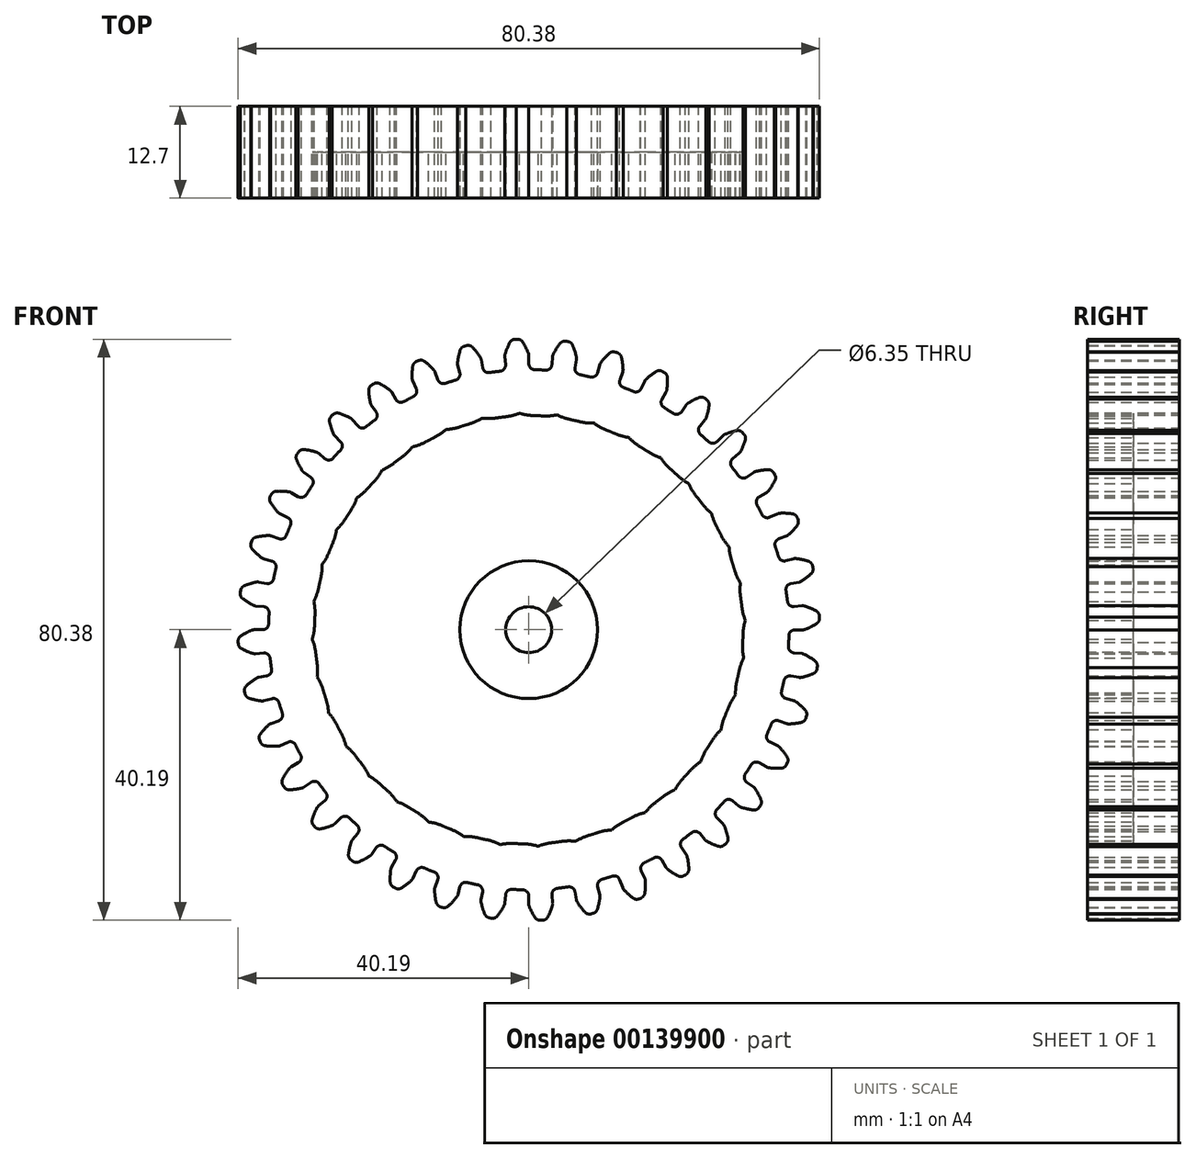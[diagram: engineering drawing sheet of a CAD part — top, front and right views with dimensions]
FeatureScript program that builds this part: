
annotation { "Feature Type Name" : "Feature", "Feature Type Description" : "" }
export const myFeature = defineFeature(function(context is Context, id is Id, definition is map)
    precondition{}
    {
        {
            assignVariable(context, id + "F0", {"name" : "CTA", "anyValue" : 5});
        }
        {
            var Q0;
            Q0=qCreatedBy(makeId("Front.planeOp"),FACE);
            var sketch = newSketch(context, id + "F1", { "sketchPlane" : qUnion([Q0])});
            skArc(sketch, "E0", {"start": v(-3.95, 35.77) * mm, "mid": v(-4.7, 35.68) * mm, "end": v(-5.44, 35.57) * mm});
            skArc(sketch, "E1.trimOffspring", {"start": v(-0.05, 38.25) * mm, "mid": v(-0.42, 39.05) * mm, "end": v(-0.86, 39.81) * mm});
            skLineSegment(sketch, "E2", {"start": v(-1.57, 40.2) * mm, "end": v(-1.75, 40.19) * mm});
            skLineSegment(sketch, "E3", {"start": v(0, 37.94) * mm, "end": v(0, 36.8) * mm});
            skLineSegment(sketch, "E4.MirrorCS", {"start": v(-1.93, 40.18) * mm, "end": v(-1.75, 40.19) * mm});
            skArc(sketch, "E5.MirrorCS", {"start": v(-3.28, 38.11) * mm, "mid": v(-2.99, 38.94) * mm, "end": v(-2.62, 39.74) * mm});
            skLineSegment(sketch, "E6.MirrorCS", {"start": v(-3.32, 37.8) * mm, "end": v(-3.22, 36.66) * mm});
            skPoint(sketch, "E7.visualSharp", {"position": v(-3.33, 37.95) * mm});
            skArc(sketch, "E7.filletArc", {"start": v(-3.28, 38.11) * mm, "mid": v(-3.31, 37.96) * mm, "end": v(-3.32, 37.8) * mm});
            skPoint(sketch, "E8.visualSharp", {"position": v(0, 38.1) * mm});
            skArc(sketch, "E8.filletArc", {"start": v(0, 37.94) * mm, "mid": v(0, 38.1) * mm, "end": v(-0.05, 38.25) * mm});
            skPoint(sketch, "E9.visualSharp", {"position": v(0, 35.98) * mm});
            skArc(sketch, "E9.filletArc", {"start": v(0, 36.8) * mm, "mid": v(0.24, 36.22) * mm, "end": v(0.82, 35.97) * mm});
            skPoint(sketch, "E10.visualSharp", {"position": v(-3.14, 35.85) * mm});
            skArc(sketch, "E10.filletArc", {"start": v(-3.95, 35.77) * mm, "mid": v(-3.4, 36.06) * mm, "end": v(-3.22, 36.66) * mm});
            skPoint(sketch, "E11.visualSharp", {"position": v(-2.39, 40.15) * mm});
            skArc(sketch, "E11.filletArc", {"start": v(-1.93, 40.18) * mm, "mid": v(-2.33, 40.05) * mm, "end": v(-2.62, 39.74) * mm});
            skPoint(sketch, "E12.visualSharp", {"position": v(-1.12, 40.2) * mm});
            skArc(sketch, "E12.filletArc", {"start": v(-0.86, 39.81) * mm, "mid": v(-1.17, 40.1) * mm, "end": v(-1.57, 40.2) * mm});
            skArc(sketch, "E13.1.0", {"start": v(-10.1, 34.54) * mm, "mid": v(-9.61, 34.92) * mm, "end": v(-9.53, 35.54) * mm});
            skLineSegment(sketch, "E13.1.1", {"start": v(-9.83, 36.65) * mm, "end": v(-9.53, 35.54) * mm});
            skArc(sketch, "E13.1.2", {"start": v(-9.85, 36.96) * mm, "mid": v(-9.7, 37.83) * mm, "end": v(-9.48, 38.68) * mm});
            skArc(sketch, "E13.1.3", {"start": v(-8.88, 39.23) * mm, "mid": v(-9.25, 39.03) * mm, "end": v(-9.48, 38.68) * mm});
            skLineSegment(sketch, "E13.1.4", {"start": v(-8.88, 39.23) * mm, "end": v(-8.7, 39.27) * mm});
            skLineSegment(sketch, "E13.1.5", {"start": v(-8.53, 39.3) * mm, "end": v(-8.7, 39.27) * mm});
            skArc(sketch, "E13.1.6", {"start": v(-7.76, 39.06) * mm, "mid": v(-8.11, 39.29) * mm, "end": v(-8.53, 39.3) * mm});
            skArc(sketch, "E13.1.7", {"start": v(-6.7, 37.66) * mm, "mid": v(-7.2, 38.39) * mm, "end": v(-7.76, 39.06) * mm});
            skLineSegment(sketch, "E13.1.8", {"start": v(-6.58, 37.37) * mm, "end": v(-6.38, 36.24) * mm});
            skArc(sketch, "E13.1.9", {"start": v(-6.38, 36.24) * mm, "mid": v(-6.05, 35.71) * mm, "end": v(-5.44, 35.57) * mm});
            skArc(sketch, "E13.1.10", {"start": v(-6.58, 37.37) * mm, "mid": v(-6.62, 37.52) * mm, "end": v(-6.7, 37.66) * mm});
            skPoint(sketch, "E13.1.11", {"position": v(-9.87, 36.8) * mm});
            skArc(sketch, "E13.1.12", {"start": v(-9.85, 36.96) * mm, "mid": v(-9.85, 36.8) * mm, "end": v(-9.83, 36.65) * mm});
            skArc(sketch, "E13.2.0", {"start": v(-15.94, 32.26) * mm, "mid": v(-15.53, 32.73) * mm, "end": v(-15.56, 33.35) * mm});
            skLineSegment(sketch, "E13.2.1", {"start": v(-16.04, 34.38) * mm, "end": v(-15.56, 33.35) * mm});
            skArc(sketch, "E13.2.2", {"start": v(-16.12, 34.7) * mm, "mid": v(-16.12, 35.57) * mm, "end": v(-16.05, 36.44) * mm});
            skArc(sketch, "E13.2.3", {"start": v(-15.56, 37.1) * mm, "mid": v(-15.89, 36.83) * mm, "end": v(-16.05, 36.44) * mm});
            skLineSegment(sketch, "E13.2.4", {"start": v(-15.56, 37.1) * mm, "end": v(-15.4, 37.16) * mm});
            skLineSegment(sketch, "E13.2.5", {"start": v(-15.23, 37.23) * mm, "end": v(-15.4, 37.16) * mm});
            skArc(sketch, "E13.2.6", {"start": v(-14.42, 37.12) * mm, "mid": v(-14.8, 37.28) * mm, "end": v(-15.23, 37.23) * mm});
            skArc(sketch, "E13.2.7", {"start": v(-13.13, 35.93) * mm, "mid": v(-13.75, 36.55) * mm, "end": v(-14.42, 37.12) * mm});
            skLineSegment(sketch, "E13.2.8", {"start": v(-12.97, 35.66) * mm, "end": v(-12.58, 34.58) * mm});
            skArc(sketch, "E13.2.9", {"start": v(-12.58, 34.58) * mm, "mid": v(-12.16, 34.12) * mm, "end": v(-11.54, 34.08) * mm});
            skArc(sketch, "E13.2.10", {"start": v(-12.97, 35.66) * mm, "mid": v(-13.04, 35.8) * mm, "end": v(-13.13, 35.93) * mm});
            skPoint(sketch, "E13.2.11", {"position": v(-16.1, 34.53) * mm});
            skArc(sketch, "E13.2.12", {"start": v(-16.12, 34.7) * mm, "mid": v(-16.1, 34.53) * mm, "end": v(-16.04, 34.38) * mm});
            skArc(sketch, "E13.3.0", {"start": v(-21.3, 29) * mm, "mid": v(-20.98, 29.53) * mm, "end": v(-21.11, 30.14) * mm});
            skLineSegment(sketch, "E13.3.1", {"start": v(-21.77, 31.08) * mm, "end": v(-21.11, 30.14) * mm});
            skArc(sketch, "E13.3.2", {"start": v(-21.9, 31.36) * mm, "mid": v(-22.06, 32.23) * mm, "end": v(-22.13, 33.1) * mm});
            skArc(sketch, "E13.3.3", {"start": v(-21.76, 33.83) * mm, "mid": v(-22.04, 33.51) * mm, "end": v(-22.13, 33.1) * mm});
            skLineSegment(sketch, "E13.3.4", {"start": v(-21.76, 33.83) * mm, "end": v(-21.61, 33.93) * mm});
            skLineSegment(sketch, "E13.3.5", {"start": v(-21.46, 34.02) * mm, "end": v(-21.61, 33.93) * mm});
            skArc(sketch, "E13.3.6", {"start": v(-20.65, 34.05) * mm, "mid": v(-21.06, 34.14) * mm, "end": v(-21.46, 34.02) * mm});
            skArc(sketch, "E13.3.7", {"start": v(-19.17, 33.1) * mm, "mid": v(-19.89, 33.61) * mm, "end": v(-20.65, 34.05) * mm});
            skLineSegment(sketch, "E13.3.8", {"start": v(-18.96, 32.86) * mm, "end": v(-18.4, 31.87) * mm});
            skArc(sketch, "E13.3.9", {"start": v(-18.4, 31.87) * mm, "mid": v(-17.9, 31.5) * mm, "end": v(-17.28, 31.56) * mm});
            skArc(sketch, "E13.3.10", {"start": v(-18.96, 32.86) * mm, "mid": v(-19.06, 33) * mm, "end": v(-19.17, 33.1) * mm});
            skPoint(sketch, "E13.3.11", {"position": v(-21.86, 31.2) * mm});
            skArc(sketch, "E13.3.12", {"start": v(-21.9, 31.36) * mm, "mid": v(-21.85, 31.21) * mm, "end": v(-21.77, 31.08) * mm});
            skArc(sketch, "E13.4.0", {"start": v(-26.01, 24.86) * mm, "mid": v(-25.79, 25.44) * mm, "end": v(-26.03, 26.01) * mm});
            skLineSegment(sketch, "E13.4.1", {"start": v(-26.84, 26.82) * mm, "end": v(-26.03, 26.01) * mm});
            skArc(sketch, "E13.4.2", {"start": v(-27.01, 27.09) * mm, "mid": v(-27.32, 27.9) * mm, "end": v(-27.55, 28.76) * mm});
            skArc(sketch, "E13.4.3", {"start": v(-27.3, 29.53) * mm, "mid": v(-27.53, 29.18) * mm, "end": v(-27.55, 28.76) * mm});
            skLineSegment(sketch, "E13.4.4", {"start": v(-27.3, 29.53) * mm, "end": v(-27.18, 29.66) * mm});
            skLineSegment(sketch, "E13.4.5", {"start": v(-27.04, 29.78) * mm, "end": v(-27.18, 29.66) * mm});
            skArc(sketch, "E13.4.6", {"start": v(-26.25, 29.95) * mm, "mid": v(-26.67, 29.97) * mm, "end": v(-27.04, 29.78) * mm});
            skArc(sketch, "E13.4.7", {"start": v(-24.63, 29.27) * mm, "mid": v(-25.42, 29.65) * mm, "end": v(-26.25, 29.95) * mm});
            skLineSegment(sketch, "E13.4.8", {"start": v(-24.38, 29.07) * mm, "end": v(-23.65, 28.2) * mm});
            skArc(sketch, "E13.4.9", {"start": v(-23.65, 28.2) * mm, "mid": v(-23.1, 27.9) * mm, "end": v(-22.5, 28.08) * mm});
            skArc(sketch, "E13.4.10", {"start": v(-24.38, 29.07) * mm, "mid": v(-24.5, 29.18) * mm, "end": v(-24.63, 29.27) * mm});
            skPoint(sketch, "E13.4.11", {"position": v(-26.95, 26.93) * mm});
            skArc(sketch, "E13.4.12", {"start": v(-27.01, 27.09) * mm, "mid": v(-26.94, 26.95) * mm, "end": v(-26.84, 26.82) * mm});
            skArc(sketch, "E13.5.0", {"start": v(-29.94, 19.97) * mm, "mid": v(-29.81, 20.58) * mm, "end": v(-30.15, 21.1) * mm});
            skLineSegment(sketch, "E13.5.1", {"start": v(-31.09, 21.76) * mm, "end": v(-30.15, 21.1) * mm});
            skArc(sketch, "E13.5.2", {"start": v(-31.3, 21.98) * mm, "mid": v(-31.75, 22.74) * mm, "end": v(-32.12, 23.54) * mm});
            skArc(sketch, "E13.5.3", {"start": v(-32.02, 24.34) * mm, "mid": v(-32.18, 23.95) * mm, "end": v(-32.12, 23.54) * mm});
            skLineSegment(sketch, "E13.5.4", {"start": v(-32.02, 24.34) * mm, "end": v(-31.91, 24.49) * mm});
            skLineSegment(sketch, "E13.5.5", {"start": v(-31.8, 24.63) * mm, "end": v(-31.91, 24.49) * mm});
            skArc(sketch, "E13.5.6", {"start": v(-31.05, 24.93) * mm, "mid": v(-31.47, 24.88) * mm, "end": v(-31.8, 24.63) * mm});
            skArc(sketch, "E13.5.7", {"start": v(-29.34, 24.55) * mm, "mid": v(-30.18, 24.78) * mm, "end": v(-31.05, 24.93) * mm});
            skLineSegment(sketch, "E13.5.8", {"start": v(-29.06, 24.4) * mm, "end": v(-28.18, 23.66) * mm});
            skArc(sketch, "E13.5.9", {"start": v(-28.18, 23.66) * mm, "mid": v(-27.6, 23.47) * mm, "end": v(-27.03, 23.75) * mm});
            skArc(sketch, "E13.5.10", {"start": v(-29.06, 24.4) * mm, "mid": v(-29.2, 24.49) * mm, "end": v(-29.34, 24.55) * mm});
            skPoint(sketch, "E13.5.11", {"position": v(-31.21, 21.85) * mm});
            skArc(sketch, "E13.5.12", {"start": v(-31.3, 21.98) * mm, "mid": v(-31.2, 21.86) * mm, "end": v(-31.09, 21.76) * mm});
            skArc(sketch, "E13.6.0", {"start": v(-32.95, 14.46) * mm, "mid": v(-32.93, 15.09) * mm, "end": v(-33.36, 15.54) * mm});
            skLineSegment(sketch, "E13.6.1", {"start": v(-34.4, 16.03) * mm, "end": v(-33.36, 15.54) * mm});
            skArc(sketch, "E13.6.2", {"start": v(-34.65, 16.21) * mm, "mid": v(-35.22, 16.88) * mm, "end": v(-35.72, 17.6) * mm});
            skArc(sketch, "E13.6.3", {"start": v(-35.76, 18.41) * mm, "mid": v(-35.85, 18) * mm, "end": v(-35.72, 17.6) * mm});
            skLineSegment(sketch, "E13.6.4", {"start": v(-35.76, 18.41) * mm, "end": v(-35.68, 18.57) * mm});
            skLineSegment(sketch, "E13.6.5", {"start": v(-35.6, 18.73) * mm, "end": v(-35.68, 18.57) * mm});
            skArc(sketch, "E13.6.6", {"start": v(-34.9, 19.16) * mm, "mid": v(-35.3, 19.04) * mm, "end": v(-35.6, 18.73) * mm});
            skArc(sketch, "E13.6.7", {"start": v(-33.15, 19.08) * mm, "mid": v(-34.03, 19.16) * mm, "end": v(-34.9, 19.16) * mm});
            skLineSegment(sketch, "E13.6.8", {"start": v(-32.86, 18.98) * mm, "end": v(-31.86, 18.4) * mm});
            skArc(sketch, "E13.6.9", {"start": v(-31.86, 18.4) * mm, "mid": v(-31.25, 18.32) * mm, "end": v(-30.75, 18.7) * mm});
            skArc(sketch, "E13.6.10", {"start": v(-32.86, 18.98) * mm, "mid": v(-33, 19.04) * mm, "end": v(-33.15, 19.08) * mm});
            skPoint(sketch, "E13.6.11", {"position": v(-34.53, 16.1) * mm});
            skArc(sketch, "E13.6.12", {"start": v(-34.65, 16.21) * mm, "mid": v(-34.53, 16.1) * mm, "end": v(-34.4, 16.03) * mm});
            skArc(sketch, "E13.7.0", {"start": v(-34.96, 8.52) * mm, "mid": v(-35.05, 9.14) * mm, "end": v(-35.55, 9.52) * mm});
            skLineSegment(sketch, "E13.7.1", {"start": v(-36.65, 9.81) * mm, "end": v(-35.55, 9.52) * mm});
            skArc(sketch, "E13.7.2", {"start": v(-36.94, 9.95) * mm, "mid": v(-37.61, 10.51) * mm, "end": v(-38.23, 11.13) * mm});
            skArc(sketch, "E13.7.3", {"start": v(-38.42, 11.92) * mm, "mid": v(-38.43, 11.5) * mm, "end": v(-38.23, 11.13) * mm});
            skLineSegment(sketch, "E13.7.4", {"start": v(-38.42, 11.92) * mm, "end": v(-38.36, 12.1) * mm});
            skLineSegment(sketch, "E13.7.5", {"start": v(-38.3, 12.27) * mm, "end": v(-38.36, 12.1) * mm});
            skArc(sketch, "E13.7.6", {"start": v(-37.7, 12.81) * mm, "mid": v(-38.08, 12.62) * mm, "end": v(-38.3, 12.27) * mm});
            skArc(sketch, "E13.7.7", {"start": v(-35.96, 13.03) * mm, "mid": v(-36.84, 12.96) * mm, "end": v(-37.7, 12.81) * mm});
            skLineSegment(sketch, "E13.7.8", {"start": v(-35.65, 12.99) * mm, "end": v(-34.58, 12.6) * mm});
            skArc(sketch, "E13.7.9", {"start": v(-34.58, 12.6) * mm, "mid": v(-33.95, 12.62) * mm, "end": v(-33.53, 13.07) * mm});
            skArc(sketch, "E13.7.10", {"start": v(-35.65, 12.99) * mm, "mid": v(-35.8, 13.03) * mm, "end": v(-35.96, 13.03) * mm});
            skPoint(sketch, "E13.7.11", {"position": v(-36.8, 9.85) * mm});
            skArc(sketch, "E13.7.12", {"start": v(-36.94, 9.95) * mm, "mid": v(-36.8, 9.87) * mm, "end": v(-36.65, 9.81) * mm});
            skArc(sketch, "E13.8.0", {"start": v(-35.9, 2.32) * mm, "mid": v(-36.1, 2.91) * mm, "end": v(-36.66, 3.2) * mm});
            skLineSegment(sketch, "E13.8.1", {"start": v(-37.8, 3.3) * mm, "end": v(-36.66, 3.2) * mm});
            skArc(sketch, "E13.8.2", {"start": v(-38.1, 3.39) * mm, "mid": v(-38.87, 3.82) * mm, "end": v(-39.59, 4.32) * mm});
            skArc(sketch, "E13.8.3", {"start": v(-39.9, 5.07) * mm, "mid": v(-39.84, 4.66) * mm, "end": v(-39.59, 4.32) * mm});
            skLineSegment(sketch, "E13.8.4", {"start": v(-39.9, 5.07) * mm, "end": v(-39.88, 5.25) * mm});
            skLineSegment(sketch, "E13.8.5", {"start": v(-39.86, 5.43) * mm, "end": v(-39.88, 5.25) * mm});
            skArc(sketch, "E13.8.6", {"start": v(-39.36, 6.07) * mm, "mid": v(-39.7, 5.82) * mm, "end": v(-39.86, 5.43) * mm});
            skArc(sketch, "E13.8.7", {"start": v(-37.68, 6.6) * mm, "mid": v(-38.53, 6.37) * mm, "end": v(-39.36, 6.07) * mm});
            skLineSegment(sketch, "E13.8.8", {"start": v(-37.37, 6.6) * mm, "end": v(-36.24, 6.4) * mm});
            skArc(sketch, "E13.8.9", {"start": v(-36.24, 6.4) * mm, "mid": v(-35.63, 6.53) * mm, "end": v(-35.29, 7.05) * mm});
            skArc(sketch, "E13.8.10", {"start": v(-37.37, 6.6) * mm, "mid": v(-37.52, 6.6) * mm, "end": v(-37.68, 6.6) * mm});
            skPoint(sketch, "E13.8.11", {"position": v(-37.96, 3.31) * mm});
            skArc(sketch, "E13.8.12", {"start": v(-38.1, 3.39) * mm, "mid": v(-37.96, 3.33) * mm, "end": v(-37.8, 3.3) * mm});
            skArc(sketch, "E13.9.0", {"start": v(-35.77, -3.95) * mm, "mid": v(-36.06, -3.4) * mm, "end": v(-36.66, -3.22) * mm});
            skLineSegment(sketch, "E13.9.1", {"start": v(-37.8, -3.32) * mm, "end": v(-36.66, -3.22) * mm});
            skArc(sketch, "E13.9.2", {"start": v(-38.11, -3.28) * mm, "mid": v(-38.94, -2.99) * mm, "end": v(-39.74, -2.62) * mm});
            skArc(sketch, "E13.9.3", {"start": v(-40.18, -1.93) * mm, "mid": v(-40.05, -2.33) * mm, "end": v(-39.74, -2.62) * mm});
            skLineSegment(sketch, "E13.9.4", {"start": v(-40.18, -1.93) * mm, "end": v(-40.19, -1.75) * mm});
            skLineSegment(sketch, "E13.9.5", {"start": v(-40.2, -1.57) * mm, "end": v(-40.19, -1.75) * mm});
            skArc(sketch, "E13.9.6", {"start": v(-39.81, -0.86) * mm, "mid": v(-40.1, -1.17) * mm, "end": v(-40.2, -1.57) * mm});
            skArc(sketch, "E13.9.7", {"start": v(-38.25, -0.05) * mm, "mid": v(-39.05, -0.42) * mm, "end": v(-39.81, -0.86) * mm});
            skLineSegment(sketch, "E13.9.8", {"start": v(-37.94, 0) * mm, "end": v(-36.8, 0) * mm});
            skArc(sketch, "E13.9.9", {"start": v(-36.8, 0) * mm, "mid": v(-36.22, 0.24) * mm, "end": v(-35.97, 0.82) * mm});
            skArc(sketch, "E13.9.10", {"start": v(-37.94, 0) * mm, "mid": v(-38.1, 0) * mm, "end": v(-38.25, -0.05) * mm});
            skPoint(sketch, "E13.9.11", {"position": v(-37.95, -3.33) * mm});
            skArc(sketch, "E13.9.12", {"start": v(-38.11, -3.28) * mm, "mid": v(-37.96, -3.31) * mm, "end": v(-37.8, -3.32) * mm});
            skArc(sketch, "E13.10.0", {"start": v(-34.54, -10.1) * mm, "mid": v(-34.92, -9.61) * mm, "end": v(-35.54, -9.53) * mm});
            skLineSegment(sketch, "E13.10.1", {"start": v(-36.65, -9.83) * mm, "end": v(-35.54, -9.53) * mm});
            skArc(sketch, "E13.10.2", {"start": v(-36.96, -9.85) * mm, "mid": v(-37.83, -9.7) * mm, "end": v(-38.68, -9.48) * mm});
            skArc(sketch, "E13.10.3", {"start": v(-39.23, -8.88) * mm, "mid": v(-39.03, -9.25) * mm, "end": v(-38.68, -9.48) * mm});
            skLineSegment(sketch, "E13.10.4", {"start": v(-39.23, -8.88) * mm, "end": v(-39.27, -8.7) * mm});
            skLineSegment(sketch, "E13.10.5", {"start": v(-39.3, -8.53) * mm, "end": v(-39.27, -8.7) * mm});
            skArc(sketch, "E13.10.6", {"start": v(-39.06, -7.76) * mm, "mid": v(-39.29, -8.11) * mm, "end": v(-39.3, -8.53) * mm});
            skArc(sketch, "E13.10.7", {"start": v(-37.66, -6.7) * mm, "mid": v(-38.39, -7.2) * mm, "end": v(-39.06, -7.76) * mm});
            skLineSegment(sketch, "E13.10.8", {"start": v(-37.37, -6.58) * mm, "end": v(-36.24, -6.38) * mm});
            skArc(sketch, "E13.10.9", {"start": v(-36.24, -6.38) * mm, "mid": v(-35.71, -6.05) * mm, "end": v(-35.57, -5.44) * mm});
            skArc(sketch, "E13.10.10", {"start": v(-37.37, -6.58) * mm, "mid": v(-37.52, -6.62) * mm, "end": v(-37.66, -6.7) * mm});
            skPoint(sketch, "E13.10.11", {"position": v(-36.8, -9.87) * mm});
            skArc(sketch, "E13.10.12", {"start": v(-36.96, -9.85) * mm, "mid": v(-36.8, -9.85) * mm, "end": v(-36.65, -9.83) * mm});
            skArc(sketch, "E13.11.0", {"start": v(-32.26, -15.94) * mm, "mid": v(-32.73, -15.53) * mm, "end": v(-33.35, -15.56) * mm});
            skLineSegment(sketch, "E13.11.1", {"start": v(-34.38, -16.04) * mm, "end": v(-33.35, -15.56) * mm});
            skArc(sketch, "E13.11.2", {"start": v(-34.7, -16.12) * mm, "mid": v(-35.57, -16.12) * mm, "end": v(-36.44, -16.05) * mm});
            skArc(sketch, "E13.11.3", {"start": v(-37.1, -15.56) * mm, "mid": v(-36.83, -15.89) * mm, "end": v(-36.44, -16.05) * mm});
            skLineSegment(sketch, "E13.11.4", {"start": v(-37.1, -15.56) * mm, "end": v(-37.16, -15.4) * mm});
            skLineSegment(sketch, "E13.11.5", {"start": v(-37.23, -15.23) * mm, "end": v(-37.16, -15.4) * mm});
            skArc(sketch, "E13.11.6", {"start": v(-37.12, -14.42) * mm, "mid": v(-37.28, -14.8) * mm, "end": v(-37.23, -15.23) * mm});
            skArc(sketch, "E13.11.7", {"start": v(-35.93, -13.13) * mm, "mid": v(-36.55, -13.75) * mm, "end": v(-37.12, -14.42) * mm});
            skLineSegment(sketch, "E13.11.8", {"start": v(-35.66, -12.97) * mm, "end": v(-34.58, -12.58) * mm});
            skArc(sketch, "E13.11.9", {"start": v(-34.58, -12.58) * mm, "mid": v(-34.12, -12.16) * mm, "end": v(-34.08, -11.54) * mm});
            skArc(sketch, "E13.11.10", {"start": v(-35.66, -12.97) * mm, "mid": v(-35.8, -13.04) * mm, "end": v(-35.93, -13.13) * mm});
            skPoint(sketch, "E13.11.11", {"position": v(-34.53, -16.1) * mm});
            skArc(sketch, "E13.11.12", {"start": v(-34.7, -16.12) * mm, "mid": v(-34.53, -16.1) * mm, "end": v(-34.38, -16.04) * mm});
            skArc(sketch, "E13.12.0", {"start": v(-29, -21.3) * mm, "mid": v(-29.53, -20.98) * mm, "end": v(-30.14, -21.11) * mm});
            skLineSegment(sketch, "E13.12.1", {"start": v(-31.08, -21.77) * mm, "end": v(-30.14, -21.11) * mm});
            skArc(sketch, "E13.12.2", {"start": v(-31.36, -21.9) * mm, "mid": v(-32.23, -22.06) * mm, "end": v(-33.1, -22.13) * mm});
            skArc(sketch, "E13.12.3", {"start": v(-33.83, -21.76) * mm, "mid": v(-33.51, -22.04) * mm, "end": v(-33.1, -22.13) * mm});
            skLineSegment(sketch, "E13.12.4", {"start": v(-33.83, -21.76) * mm, "end": v(-33.93, -21.61) * mm});
            skLineSegment(sketch, "E13.12.5", {"start": v(-34.02, -21.46) * mm, "end": v(-33.93, -21.61) * mm});
            skArc(sketch, "E13.12.6", {"start": v(-34.05, -20.65) * mm, "mid": v(-34.14, -21.06) * mm, "end": v(-34.02, -21.46) * mm});
            skArc(sketch, "E13.12.7", {"start": v(-33.1, -19.17) * mm, "mid": v(-33.61, -19.89) * mm, "end": v(-34.05, -20.65) * mm});
            skLineSegment(sketch, "E13.12.8", {"start": v(-32.86, -18.96) * mm, "end": v(-31.87, -18.4) * mm});
            skArc(sketch, "E13.12.9", {"start": v(-31.87, -18.4) * mm, "mid": v(-31.5, -17.9) * mm, "end": v(-31.56, -17.28) * mm});
            skArc(sketch, "E13.12.10", {"start": v(-32.86, -18.96) * mm, "mid": v(-33, -19.06) * mm, "end": v(-33.1, -19.17) * mm});
            skPoint(sketch, "E13.12.11", {"position": v(-31.2, -21.86) * mm});
            skArc(sketch, "E13.12.12", {"start": v(-31.36, -21.9) * mm, "mid": v(-31.21, -21.85) * mm, "end": v(-31.08, -21.77) * mm});
            skArc(sketch, "E13.13.0", {"start": v(-24.86, -26.01) * mm, "mid": v(-25.44, -25.79) * mm, "end": v(-26.01, -26.03) * mm});
            skLineSegment(sketch, "E13.13.1", {"start": v(-26.82, -26.84) * mm, "end": v(-26.01, -26.03) * mm});
            skArc(sketch, "E13.13.2", {"start": v(-27.09, -27.01) * mm, "mid": v(-27.9, -27.32) * mm, "end": v(-28.76, -27.55) * mm});
            skArc(sketch, "E13.13.3", {"start": v(-29.53, -27.3) * mm, "mid": v(-29.18, -27.53) * mm, "end": v(-28.76, -27.55) * mm});
            skLineSegment(sketch, "E13.13.4", {"start": v(-29.53, -27.3) * mm, "end": v(-29.66, -27.18) * mm});
            skLineSegment(sketch, "E13.13.5", {"start": v(-29.78, -27.04) * mm, "end": v(-29.66, -27.18) * mm});
            skArc(sketch, "E13.13.6", {"start": v(-29.95, -26.25) * mm, "mid": v(-29.97, -26.67) * mm, "end": v(-29.78, -27.04) * mm});
            skArc(sketch, "E13.13.7", {"start": v(-29.27, -24.63) * mm, "mid": v(-29.65, -25.42) * mm, "end": v(-29.95, -26.25) * mm});
            skLineSegment(sketch, "E13.13.8", {"start": v(-29.07, -24.38) * mm, "end": v(-28.2, -23.65) * mm});
            skArc(sketch, "E13.13.9", {"start": v(-28.2, -23.65) * mm, "mid": v(-27.9, -23.1) * mm, "end": v(-28.08, -22.5) * mm});
            skArc(sketch, "E13.13.10", {"start": v(-29.07, -24.38) * mm, "mid": v(-29.18, -24.5) * mm, "end": v(-29.27, -24.63) * mm});
            skPoint(sketch, "E13.13.11", {"position": v(-26.93, -26.95) * mm});
            skArc(sketch, "E13.13.12", {"start": v(-27.09, -27.01) * mm, "mid": v(-26.95, -26.94) * mm, "end": v(-26.82, -26.84) * mm});
            skArc(sketch, "E13.14.0", {"start": v(-19.97, -29.94) * mm, "mid": v(-20.58, -29.81) * mm, "end": v(-21.1, -30.15) * mm});
            skLineSegment(sketch, "E13.14.1", {"start": v(-21.76, -31.09) * mm, "end": v(-21.1, -30.15) * mm});
            skArc(sketch, "E13.14.2", {"start": v(-21.98, -31.3) * mm, "mid": v(-22.74, -31.75) * mm, "end": v(-23.54, -32.12) * mm});
            skArc(sketch, "E13.14.3", {"start": v(-24.34, -32.02) * mm, "mid": v(-23.95, -32.18) * mm, "end": v(-23.54, -32.12) * mm});
            skLineSegment(sketch, "E13.14.4", {"start": v(-24.34, -32.02) * mm, "end": v(-24.49, -31.91) * mm});
            skLineSegment(sketch, "E13.14.5", {"start": v(-24.63, -31.8) * mm, "end": v(-24.49, -31.91) * mm});
            skArc(sketch, "E13.14.6", {"start": v(-24.93, -31.05) * mm, "mid": v(-24.88, -31.47) * mm, "end": v(-24.63, -31.8) * mm});
            skArc(sketch, "E13.14.7", {"start": v(-24.55, -29.34) * mm, "mid": v(-24.78, -30.18) * mm, "end": v(-24.93, -31.05) * mm});
            skLineSegment(sketch, "E13.14.8", {"start": v(-24.4, -29.06) * mm, "end": v(-23.66, -28.18) * mm});
            skArc(sketch, "E13.14.9", {"start": v(-23.66, -28.18) * mm, "mid": v(-23.47, -27.6) * mm, "end": v(-23.75, -27.03) * mm});
            skArc(sketch, "E13.14.10", {"start": v(-24.4, -29.06) * mm, "mid": v(-24.49, -29.2) * mm, "end": v(-24.55, -29.34) * mm});
            skPoint(sketch, "E13.14.11", {"position": v(-21.85, -31.21) * mm});
            skArc(sketch, "E13.14.12", {"start": v(-21.98, -31.3) * mm, "mid": v(-21.86, -31.2) * mm, "end": v(-21.76, -31.09) * mm});
            skArc(sketch, "E13.15.0", {"start": v(-14.46, -32.95) * mm, "mid": v(-15.09, -32.93) * mm, "end": v(-15.54, -33.36) * mm});
            skLineSegment(sketch, "E13.15.1", {"start": v(-16.03, -34.4) * mm, "end": v(-15.54, -33.36) * mm});
            skArc(sketch, "E13.15.2", {"start": v(-16.21, -34.65) * mm, "mid": v(-16.88, -35.22) * mm, "end": v(-17.6, -35.72) * mm});
            skArc(sketch, "E13.15.3", {"start": v(-18.41, -35.76) * mm, "mid": v(-18, -35.85) * mm, "end": v(-17.6, -35.72) * mm});
            skLineSegment(sketch, "E13.15.4", {"start": v(-18.41, -35.76) * mm, "end": v(-18.57, -35.68) * mm});
            skLineSegment(sketch, "E13.15.5", {"start": v(-18.73, -35.6) * mm, "end": v(-18.57, -35.68) * mm});
            skArc(sketch, "E13.15.6", {"start": v(-19.16, -34.9) * mm, "mid": v(-19.04, -35.3) * mm, "end": v(-18.73, -35.6) * mm});
            skArc(sketch, "E13.15.7", {"start": v(-19.08, -33.15) * mm, "mid": v(-19.16, -34.03) * mm, "end": v(-19.16, -34.9) * mm});
            skLineSegment(sketch, "E13.15.8", {"start": v(-18.98, -32.86) * mm, "end": v(-18.4, -31.86) * mm});
            skArc(sketch, "E13.15.9", {"start": v(-18.4, -31.86) * mm, "mid": v(-18.32, -31.25) * mm, "end": v(-18.7, -30.75) * mm});
            skArc(sketch, "E13.15.10", {"start": v(-18.98, -32.86) * mm, "mid": v(-19.04, -33) * mm, "end": v(-19.08, -33.15) * mm});
            skPoint(sketch, "E13.15.11", {"position": v(-16.1, -34.53) * mm});
            skArc(sketch, "E13.15.12", {"start": v(-16.21, -34.65) * mm, "mid": v(-16.1, -34.53) * mm, "end": v(-16.03, -34.4) * mm});
            skArc(sketch, "E13.16.0", {"start": v(-8.52, -34.96) * mm, "mid": v(-9.14, -35.05) * mm, "end": v(-9.52, -35.55) * mm});
            skLineSegment(sketch, "E13.16.1", {"start": v(-9.81, -36.65) * mm, "end": v(-9.52, -35.55) * mm});
            skArc(sketch, "E13.16.2", {"start": v(-9.95, -36.94) * mm, "mid": v(-10.51, -37.61) * mm, "end": v(-11.13, -38.23) * mm});
            skArc(sketch, "E13.16.3", {"start": v(-11.92, -38.42) * mm, "mid": v(-11.5, -38.43) * mm, "end": v(-11.13, -38.23) * mm});
            skLineSegment(sketch, "E13.16.4", {"start": v(-11.92, -38.42) * mm, "end": v(-12.1, -38.36) * mm});
            skLineSegment(sketch, "E13.16.5", {"start": v(-12.27, -38.3) * mm, "end": v(-12.1, -38.36) * mm});
            skArc(sketch, "E13.16.6", {"start": v(-12.81, -37.7) * mm, "mid": v(-12.62, -38.08) * mm, "end": v(-12.27, -38.3) * mm});
            skArc(sketch, "E13.16.7", {"start": v(-13.03, -35.96) * mm, "mid": v(-12.96, -36.84) * mm, "end": v(-12.81, -37.7) * mm});
            skLineSegment(sketch, "E13.16.8", {"start": v(-12.99, -35.65) * mm, "end": v(-12.6, -34.58) * mm});
            skArc(sketch, "E13.16.9", {"start": v(-12.6, -34.58) * mm, "mid": v(-12.62, -33.95) * mm, "end": v(-13.07, -33.53) * mm});
            skArc(sketch, "E13.16.10", {"start": v(-12.99, -35.65) * mm, "mid": v(-13.03, -35.8) * mm, "end": v(-13.03, -35.96) * mm});
            skPoint(sketch, "E13.16.11", {"position": v(-9.85, -36.8) * mm});
            skArc(sketch, "E13.16.12", {"start": v(-9.95, -36.94) * mm, "mid": v(-9.87, -36.8) * mm, "end": v(-9.81, -36.65) * mm});
            skArc(sketch, "E13.17.0", {"start": v(-2.32, -35.9) * mm, "mid": v(-2.91, -36.1) * mm, "end": v(-3.2, -36.66) * mm});
            skLineSegment(sketch, "E13.17.1", {"start": v(-3.3, -37.8) * mm, "end": v(-3.2, -36.66) * mm});
            skArc(sketch, "E13.17.2", {"start": v(-3.39, -38.1) * mm, "mid": v(-3.82, -38.87) * mm, "end": v(-4.32, -39.59) * mm});
            skArc(sketch, "E13.17.3", {"start": v(-5.07, -39.9) * mm, "mid": v(-4.66, -39.84) * mm, "end": v(-4.32, -39.59) * mm});
            skLineSegment(sketch, "E13.17.4", {"start": v(-5.07, -39.9) * mm, "end": v(-5.25, -39.88) * mm});
            skLineSegment(sketch, "E13.17.5", {"start": v(-5.43, -39.86) * mm, "end": v(-5.25, -39.88) * mm});
            skArc(sketch, "E13.17.6", {"start": v(-6.07, -39.36) * mm, "mid": v(-5.82, -39.7) * mm, "end": v(-5.43, -39.86) * mm});
            skArc(sketch, "E13.17.7", {"start": v(-6.6, -37.68) * mm, "mid": v(-6.37, -38.53) * mm, "end": v(-6.07, -39.36) * mm});
            skLineSegment(sketch, "E13.17.8", {"start": v(-6.6, -37.37) * mm, "end": v(-6.4, -36.24) * mm});
            skArc(sketch, "E13.17.9", {"start": v(-6.4, -36.24) * mm, "mid": v(-6.53, -35.63) * mm, "end": v(-7.05, -35.29) * mm});
            skArc(sketch, "E13.17.10", {"start": v(-6.6, -37.37) * mm, "mid": v(-6.6, -37.52) * mm, "end": v(-6.6, -37.68) * mm});
            skPoint(sketch, "E13.17.11", {"position": v(-3.31, -37.96) * mm});
            skArc(sketch, "E13.17.12", {"start": v(-3.39, -38.1) * mm, "mid": v(-3.33, -37.96) * mm, "end": v(-3.3, -37.8) * mm});
            skArc(sketch, "E13.18.0", {"start": v(3.95, -35.77) * mm, "mid": v(3.4, -36.06) * mm, "end": v(3.22, -36.66) * mm});
            skLineSegment(sketch, "E13.18.1", {"start": v(3.32, -37.8) * mm, "end": v(3.22, -36.66) * mm});
            skArc(sketch, "E13.18.2", {"start": v(3.28, -38.11) * mm, "mid": v(2.99, -38.94) * mm, "end": v(2.62, -39.74) * mm});
            skArc(sketch, "E13.18.3", {"start": v(1.93, -40.18) * mm, "mid": v(2.33, -40.05) * mm, "end": v(2.62, -39.74) * mm});
            skLineSegment(sketch, "E13.18.4", {"start": v(1.93, -40.18) * mm, "end": v(1.75, -40.19) * mm});
            skLineSegment(sketch, "E13.18.5", {"start": v(1.57, -40.2) * mm, "end": v(1.75, -40.19) * mm});
            skArc(sketch, "E13.18.6", {"start": v(0.86, -39.81) * mm, "mid": v(1.17, -40.1) * mm, "end": v(1.57, -40.2) * mm});
            skArc(sketch, "E13.18.7", {"start": v(0.05, -38.25) * mm, "mid": v(0.42, -39.05) * mm, "end": v(0.86, -39.81) * mm});
            skLineSegment(sketch, "E13.18.8", {"start": v(0, -37.94) * mm, "end": v(0, -36.8) * mm});
            skArc(sketch, "E13.18.9", {"start": v(0, -36.8) * mm, "mid": v(-0.24, -36.22) * mm, "end": v(-0.82, -35.97) * mm});
            skArc(sketch, "E13.18.10", {"start": v(0, -37.94) * mm, "mid": v(0, -38.1) * mm, "end": v(0.05, -38.25) * mm});
            skPoint(sketch, "E13.18.11", {"position": v(3.33, -37.95) * mm});
            skArc(sketch, "E13.18.12", {"start": v(3.28, -38.11) * mm, "mid": v(3.31, -37.96) * mm, "end": v(3.32, -37.8) * mm});
            skArc(sketch, "E13.19.0", {"start": v(10.1, -34.54) * mm, "mid": v(9.61, -34.92) * mm, "end": v(9.53, -35.54) * mm});
            skLineSegment(sketch, "E13.19.1", {"start": v(9.83, -36.65) * mm, "end": v(9.53, -35.54) * mm});
            skArc(sketch, "E13.19.2", {"start": v(9.85, -36.96) * mm, "mid": v(9.7, -37.83) * mm, "end": v(9.48, -38.68) * mm});
            skArc(sketch, "E13.19.3", {"start": v(8.88, -39.23) * mm, "mid": v(9.25, -39.03) * mm, "end": v(9.48, -38.68) * mm});
            skLineSegment(sketch, "E13.19.4", {"start": v(8.88, -39.23) * mm, "end": v(8.7, -39.27) * mm});
            skLineSegment(sketch, "E13.19.5", {"start": v(8.53, -39.3) * mm, "end": v(8.7, -39.27) * mm});
            skArc(sketch, "E13.19.6", {"start": v(7.76, -39.06) * mm, "mid": v(8.11, -39.29) * mm, "end": v(8.53, -39.3) * mm});
            skArc(sketch, "E13.19.7", {"start": v(6.7, -37.66) * mm, "mid": v(7.2, -38.39) * mm, "end": v(7.76, -39.06) * mm});
            skLineSegment(sketch, "E13.19.8", {"start": v(6.58, -37.37) * mm, "end": v(6.38, -36.24) * mm});
            skArc(sketch, "E13.19.9", {"start": v(6.38, -36.24) * mm, "mid": v(6.05, -35.71) * mm, "end": v(5.44, -35.57) * mm});
            skArc(sketch, "E13.19.10", {"start": v(6.58, -37.37) * mm, "mid": v(6.62, -37.52) * mm, "end": v(6.7, -37.66) * mm});
            skPoint(sketch, "E13.19.11", {"position": v(9.87, -36.8) * mm});
            skArc(sketch, "E13.19.12", {"start": v(9.85, -36.96) * mm, "mid": v(9.85, -36.8) * mm, "end": v(9.83, -36.65) * mm});
            skArc(sketch, "E13.20.0", {"start": v(15.94, -32.26) * mm, "mid": v(15.53, -32.73) * mm, "end": v(15.56, -33.35) * mm});
            skLineSegment(sketch, "E13.20.1", {"start": v(16.04, -34.38) * mm, "end": v(15.56, -33.35) * mm});
            skArc(sketch, "E13.20.2", {"start": v(16.12, -34.7) * mm, "mid": v(16.12, -35.57) * mm, "end": v(16.05, -36.44) * mm});
            skArc(sketch, "E13.20.3", {"start": v(15.56, -37.1) * mm, "mid": v(15.89, -36.83) * mm, "end": v(16.05, -36.44) * mm});
            skLineSegment(sketch, "E13.20.4", {"start": v(15.56, -37.1) * mm, "end": v(15.4, -37.16) * mm});
            skLineSegment(sketch, "E13.20.5", {"start": v(15.23, -37.23) * mm, "end": v(15.4, -37.16) * mm});
            skArc(sketch, "E13.20.6", {"start": v(14.42, -37.12) * mm, "mid": v(14.8, -37.28) * mm, "end": v(15.23, -37.23) * mm});
            skArc(sketch, "E13.20.7", {"start": v(13.13, -35.93) * mm, "mid": v(13.75, -36.55) * mm, "end": v(14.42, -37.12) * mm});
            skLineSegment(sketch, "E13.20.8", {"start": v(12.97, -35.66) * mm, "end": v(12.58, -34.58) * mm});
            skArc(sketch, "E13.20.9", {"start": v(12.58, -34.58) * mm, "mid": v(12.16, -34.12) * mm, "end": v(11.54, -34.08) * mm});
            skArc(sketch, "E13.20.10", {"start": v(12.97, -35.66) * mm, "mid": v(13.04, -35.8) * mm, "end": v(13.13, -35.93) * mm});
            skPoint(sketch, "E13.20.11", {"position": v(16.1, -34.53) * mm});
            skArc(sketch, "E13.20.12", {"start": v(16.12, -34.7) * mm, "mid": v(16.1, -34.53) * mm, "end": v(16.04, -34.38) * mm});
            skArc(sketch, "E13.21.0", {"start": v(21.3, -29) * mm, "mid": v(20.98, -29.53) * mm, "end": v(21.11, -30.14) * mm});
            skLineSegment(sketch, "E13.21.1", {"start": v(21.77, -31.08) * mm, "end": v(21.11, -30.14) * mm});
            skArc(sketch, "E13.21.2", {"start": v(21.9, -31.36) * mm, "mid": v(22.06, -32.23) * mm, "end": v(22.13, -33.1) * mm});
            skArc(sketch, "E13.21.3", {"start": v(21.76, -33.83) * mm, "mid": v(22.04, -33.51) * mm, "end": v(22.13, -33.1) * mm});
            skLineSegment(sketch, "E13.21.4", {"start": v(21.76, -33.83) * mm, "end": v(21.61, -33.93) * mm});
            skLineSegment(sketch, "E13.21.5", {"start": v(21.46, -34.02) * mm, "end": v(21.61, -33.93) * mm});
            skArc(sketch, "E13.21.6", {"start": v(20.65, -34.05) * mm, "mid": v(21.06, -34.14) * mm, "end": v(21.46, -34.02) * mm});
            skArc(sketch, "E13.21.7", {"start": v(19.17, -33.1) * mm, "mid": v(19.89, -33.61) * mm, "end": v(20.65, -34.05) * mm});
            skLineSegment(sketch, "E13.21.8", {"start": v(18.96, -32.86) * mm, "end": v(18.4, -31.87) * mm});
            skArc(sketch, "E13.21.9", {"start": v(18.4, -31.87) * mm, "mid": v(17.9, -31.5) * mm, "end": v(17.28, -31.56) * mm});
            skArc(sketch, "E13.21.10", {"start": v(18.96, -32.86) * mm, "mid": v(19.06, -33) * mm, "end": v(19.17, -33.1) * mm});
            skPoint(sketch, "E13.21.11", {"position": v(21.86, -31.2) * mm});
            skArc(sketch, "E13.21.12", {"start": v(21.9, -31.36) * mm, "mid": v(21.85, -31.21) * mm, "end": v(21.77, -31.08) * mm});
            skArc(sketch, "E13.22.0", {"start": v(26.01, -24.86) * mm, "mid": v(25.79, -25.44) * mm, "end": v(26.03, -26.01) * mm});
            skLineSegment(sketch, "E13.22.1", {"start": v(26.84, -26.82) * mm, "end": v(26.03, -26.01) * mm});
            skArc(sketch, "E13.22.2", {"start": v(27.01, -27.09) * mm, "mid": v(27.32, -27.9) * mm, "end": v(27.55, -28.76) * mm});
            skArc(sketch, "E13.22.3", {"start": v(27.3, -29.53) * mm, "mid": v(27.53, -29.18) * mm, "end": v(27.55, -28.76) * mm});
            skLineSegment(sketch, "E13.22.4", {"start": v(27.3, -29.53) * mm, "end": v(27.18, -29.66) * mm});
            skLineSegment(sketch, "E13.22.5", {"start": v(27.04, -29.78) * mm, "end": v(27.18, -29.66) * mm});
            skArc(sketch, "E13.22.6", {"start": v(26.25, -29.95) * mm, "mid": v(26.67, -29.97) * mm, "end": v(27.04, -29.78) * mm});
            skArc(sketch, "E13.22.7", {"start": v(24.63, -29.27) * mm, "mid": v(25.42, -29.65) * mm, "end": v(26.25, -29.95) * mm});
            skLineSegment(sketch, "E13.22.8", {"start": v(24.38, -29.07) * mm, "end": v(23.65, -28.2) * mm});
            skArc(sketch, "E13.22.9", {"start": v(23.65, -28.2) * mm, "mid": v(23.1, -27.9) * mm, "end": v(22.5, -28.08) * mm});
            skArc(sketch, "E13.22.10", {"start": v(24.38, -29.07) * mm, "mid": v(24.5, -29.18) * mm, "end": v(24.63, -29.27) * mm});
            skPoint(sketch, "E13.22.11", {"position": v(26.95, -26.93) * mm});
            skArc(sketch, "E13.22.12", {"start": v(27.01, -27.09) * mm, "mid": v(26.94, -26.95) * mm, "end": v(26.84, -26.82) * mm});
            skArc(sketch, "E13.23.0", {"start": v(29.94, -19.97) * mm, "mid": v(29.81, -20.58) * mm, "end": v(30.15, -21.1) * mm});
            skLineSegment(sketch, "E13.23.1", {"start": v(31.09, -21.76) * mm, "end": v(30.15, -21.1) * mm});
            skArc(sketch, "E13.23.2", {"start": v(31.3, -21.98) * mm, "mid": v(31.75, -22.74) * mm, "end": v(32.12, -23.54) * mm});
            skArc(sketch, "E13.23.3", {"start": v(32.02, -24.34) * mm, "mid": v(32.18, -23.95) * mm, "end": v(32.12, -23.54) * mm});
            skLineSegment(sketch, "E13.23.4", {"start": v(32.02, -24.34) * mm, "end": v(31.91, -24.49) * mm});
            skLineSegment(sketch, "E13.23.5", {"start": v(31.8, -24.63) * mm, "end": v(31.91, -24.49) * mm});
            skArc(sketch, "E13.23.6", {"start": v(31.05, -24.93) * mm, "mid": v(31.47, -24.88) * mm, "end": v(31.8, -24.63) * mm});
            skArc(sketch, "E13.23.7", {"start": v(29.34, -24.55) * mm, "mid": v(30.18, -24.78) * mm, "end": v(31.05, -24.93) * mm});
            skLineSegment(sketch, "E13.23.8", {"start": v(29.06, -24.4) * mm, "end": v(28.18, -23.66) * mm});
            skArc(sketch, "E13.23.9", {"start": v(28.18, -23.66) * mm, "mid": v(27.6, -23.47) * mm, "end": v(27.03, -23.75) * mm});
            skArc(sketch, "E13.23.10", {"start": v(29.06, -24.4) * mm, "mid": v(29.2, -24.49) * mm, "end": v(29.34, -24.55) * mm});
            skPoint(sketch, "E13.23.11", {"position": v(31.21, -21.85) * mm});
            skArc(sketch, "E13.23.12", {"start": v(31.3, -21.98) * mm, "mid": v(31.2, -21.86) * mm, "end": v(31.09, -21.76) * mm});
            skArc(sketch, "E13.24.0", {"start": v(32.95, -14.46) * mm, "mid": v(32.93, -15.09) * mm, "end": v(33.36, -15.54) * mm});
            skLineSegment(sketch, "E13.24.1", {"start": v(34.4, -16.03) * mm, "end": v(33.36, -15.54) * mm});
            skArc(sketch, "E13.24.2", {"start": v(34.65, -16.21) * mm, "mid": v(35.22, -16.88) * mm, "end": v(35.72, -17.6) * mm});
            skArc(sketch, "E13.24.3", {"start": v(35.76, -18.41) * mm, "mid": v(35.85, -18) * mm, "end": v(35.72, -17.6) * mm});
            skLineSegment(sketch, "E13.24.4", {"start": v(35.76, -18.41) * mm, "end": v(35.68, -18.57) * mm});
            skLineSegment(sketch, "E13.24.5", {"start": v(35.6, -18.73) * mm, "end": v(35.68, -18.57) * mm});
            skArc(sketch, "E13.24.6", {"start": v(34.9, -19.16) * mm, "mid": v(35.3, -19.04) * mm, "end": v(35.6, -18.73) * mm});
            skArc(sketch, "E13.24.7", {"start": v(33.15, -19.08) * mm, "mid": v(34.03, -19.16) * mm, "end": v(34.9, -19.16) * mm});
            skLineSegment(sketch, "E13.24.8", {"start": v(32.86, -18.98) * mm, "end": v(31.86, -18.4) * mm});
            skArc(sketch, "E13.24.9", {"start": v(31.86, -18.4) * mm, "mid": v(31.25, -18.32) * mm, "end": v(30.75, -18.7) * mm});
            skArc(sketch, "E13.24.10", {"start": v(32.86, -18.98) * mm, "mid": v(33, -19.04) * mm, "end": v(33.15, -19.08) * mm});
            skPoint(sketch, "E13.24.11", {"position": v(34.53, -16.1) * mm});
            skArc(sketch, "E13.24.12", {"start": v(34.65, -16.21) * mm, "mid": v(34.53, -16.1) * mm, "end": v(34.4, -16.03) * mm});
            skArc(sketch, "E13.25.0", {"start": v(34.96, -8.52) * mm, "mid": v(35.05, -9.14) * mm, "end": v(35.55, -9.52) * mm});
            skLineSegment(sketch, "E13.25.1", {"start": v(36.65, -9.81) * mm, "end": v(35.55, -9.52) * mm});
            skArc(sketch, "E13.25.2", {"start": v(36.94, -9.95) * mm, "mid": v(37.61, -10.51) * mm, "end": v(38.23, -11.13) * mm});
            skArc(sketch, "E13.25.3", {"start": v(38.42, -11.92) * mm, "mid": v(38.43, -11.5) * mm, "end": v(38.23, -11.13) * mm});
            skLineSegment(sketch, "E13.25.4", {"start": v(38.42, -11.92) * mm, "end": v(38.36, -12.1) * mm});
            skLineSegment(sketch, "E13.25.5", {"start": v(38.3, -12.27) * mm, "end": v(38.36, -12.1) * mm});
            skArc(sketch, "E13.25.6", {"start": v(37.7, -12.81) * mm, "mid": v(38.08, -12.62) * mm, "end": v(38.3, -12.27) * mm});
            skArc(sketch, "E13.25.7", {"start": v(35.96, -13.03) * mm, "mid": v(36.84, -12.96) * mm, "end": v(37.7, -12.81) * mm});
            skLineSegment(sketch, "E13.25.8", {"start": v(35.65, -12.99) * mm, "end": v(34.58, -12.6) * mm});
            skArc(sketch, "E13.25.9", {"start": v(34.58, -12.6) * mm, "mid": v(33.95, -12.62) * mm, "end": v(33.53, -13.07) * mm});
            skArc(sketch, "E13.25.10", {"start": v(35.65, -12.99) * mm, "mid": v(35.8, -13.03) * mm, "end": v(35.96, -13.03) * mm});
            skPoint(sketch, "E13.25.11", {"position": v(36.8, -9.85) * mm});
            skArc(sketch, "E13.25.12", {"start": v(36.94, -9.95) * mm, "mid": v(36.8, -9.87) * mm, "end": v(36.65, -9.81) * mm});
            skArc(sketch, "E13.26.0", {"start": v(35.9, -2.32) * mm, "mid": v(36.1, -2.91) * mm, "end": v(36.66, -3.2) * mm});
            skLineSegment(sketch, "E13.26.1", {"start": v(37.8, -3.3) * mm, "end": v(36.66, -3.2) * mm});
            skArc(sketch, "E13.26.2", {"start": v(38.1, -3.39) * mm, "mid": v(38.87, -3.82) * mm, "end": v(39.59, -4.32) * mm});
            skArc(sketch, "E13.26.3", {"start": v(39.9, -5.07) * mm, "mid": v(39.84, -4.66) * mm, "end": v(39.59, -4.32) * mm});
            skLineSegment(sketch, "E13.26.4", {"start": v(39.9, -5.07) * mm, "end": v(39.88, -5.25) * mm});
            skLineSegment(sketch, "E13.26.5", {"start": v(39.86, -5.43) * mm, "end": v(39.88, -5.25) * mm});
            skArc(sketch, "E13.26.6", {"start": v(39.36, -6.07) * mm, "mid": v(39.7, -5.82) * mm, "end": v(39.86, -5.43) * mm});
            skArc(sketch, "E13.26.7", {"start": v(37.68, -6.6) * mm, "mid": v(38.53, -6.37) * mm, "end": v(39.36, -6.07) * mm});
            skLineSegment(sketch, "E13.26.8", {"start": v(37.37, -6.6) * mm, "end": v(36.24, -6.4) * mm});
            skArc(sketch, "E13.26.9", {"start": v(36.24, -6.4) * mm, "mid": v(35.63, -6.53) * mm, "end": v(35.29, -7.05) * mm});
            skArc(sketch, "E13.26.10", {"start": v(37.37, -6.6) * mm, "mid": v(37.52, -6.6) * mm, "end": v(37.68, -6.6) * mm});
            skPoint(sketch, "E13.26.11", {"position": v(37.96, -3.31) * mm});
            skArc(sketch, "E13.26.12", {"start": v(38.1, -3.39) * mm, "mid": v(37.96, -3.33) * mm, "end": v(37.8, -3.3) * mm});
            skArc(sketch, "E13.27.0", {"start": v(35.77, 3.95) * mm, "mid": v(36.06, 3.4) * mm, "end": v(36.66, 3.22) * mm});
            skLineSegment(sketch, "E13.27.1", {"start": v(37.8, 3.32) * mm, "end": v(36.66, 3.22) * mm});
            skArc(sketch, "E13.27.2", {"start": v(38.11, 3.28) * mm, "mid": v(38.94, 2.99) * mm, "end": v(39.74, 2.62) * mm});
            skArc(sketch, "E13.27.3", {"start": v(40.18, 1.93) * mm, "mid": v(40.05, 2.33) * mm, "end": v(39.74, 2.62) * mm});
            skLineSegment(sketch, "E13.27.4", {"start": v(40.18, 1.93) * mm, "end": v(40.19, 1.75) * mm});
            skLineSegment(sketch, "E13.27.5", {"start": v(40.2, 1.57) * mm, "end": v(40.19, 1.75) * mm});
            skArc(sketch, "E13.27.6", {"start": v(39.81, 0.86) * mm, "mid": v(40.1, 1.17) * mm, "end": v(40.2, 1.57) * mm});
            skArc(sketch, "E13.27.7", {"start": v(38.25, 0.05) * mm, "mid": v(39.05, 0.42) * mm, "end": v(39.81, 0.86) * mm});
            skLineSegment(sketch, "E13.27.8", {"start": v(37.94, 0) * mm, "end": v(36.8, 0) * mm});
            skArc(sketch, "E13.27.9", {"start": v(36.8, 0) * mm, "mid": v(36.22, -0.24) * mm, "end": v(35.97, -0.82) * mm});
            skArc(sketch, "E13.27.10", {"start": v(37.94, 0) * mm, "mid": v(38.1, 0) * mm, "end": v(38.25, 0.05) * mm});
            skPoint(sketch, "E13.27.11", {"position": v(37.95, 3.33) * mm});
            skArc(sketch, "E13.27.12", {"start": v(38.11, 3.28) * mm, "mid": v(37.96, 3.31) * mm, "end": v(37.8, 3.32) * mm});
            skArc(sketch, "E13.28.0", {"start": v(34.54, 10.1) * mm, "mid": v(34.92, 9.61) * mm, "end": v(35.54, 9.53) * mm});
            skLineSegment(sketch, "E13.28.1", {"start": v(36.65, 9.83) * mm, "end": v(35.54, 9.53) * mm});
            skArc(sketch, "E13.28.2", {"start": v(36.96, 9.85) * mm, "mid": v(37.83, 9.7) * mm, "end": v(38.68, 9.48) * mm});
            skArc(sketch, "E13.28.3", {"start": v(39.23, 8.88) * mm, "mid": v(39.03, 9.25) * mm, "end": v(38.68, 9.48) * mm});
            skLineSegment(sketch, "E13.28.4", {"start": v(39.23, 8.88) * mm, "end": v(39.27, 8.7) * mm});
            skLineSegment(sketch, "E13.28.5", {"start": v(39.3, 8.53) * mm, "end": v(39.27, 8.7) * mm});
            skArc(sketch, "E13.28.6", {"start": v(39.06, 7.76) * mm, "mid": v(39.29, 8.11) * mm, "end": v(39.3, 8.53) * mm});
            skArc(sketch, "E13.28.7", {"start": v(37.66, 6.7) * mm, "mid": v(38.39, 7.2) * mm, "end": v(39.06, 7.76) * mm});
            skLineSegment(sketch, "E13.28.8", {"start": v(37.37, 6.58) * mm, "end": v(36.24, 6.38) * mm});
            skArc(sketch, "E13.28.9", {"start": v(36.24, 6.38) * mm, "mid": v(35.71, 6.05) * mm, "end": v(35.57, 5.44) * mm});
            skArc(sketch, "E13.28.10", {"start": v(37.37, 6.58) * mm, "mid": v(37.52, 6.62) * mm, "end": v(37.66, 6.7) * mm});
            skPoint(sketch, "E13.28.11", {"position": v(36.8, 9.87) * mm});
            skArc(sketch, "E13.28.12", {"start": v(36.96, 9.85) * mm, "mid": v(36.8, 9.85) * mm, "end": v(36.65, 9.83) * mm});
            skArc(sketch, "E13.29.0", {"start": v(32.26, 15.94) * mm, "mid": v(32.73, 15.53) * mm, "end": v(33.35, 15.56) * mm});
            skLineSegment(sketch, "E13.29.1", {"start": v(34.38, 16.04) * mm, "end": v(33.35, 15.56) * mm});
            skArc(sketch, "E13.29.2", {"start": v(34.7, 16.12) * mm, "mid": v(35.57, 16.12) * mm, "end": v(36.44, 16.05) * mm});
            skArc(sketch, "E13.29.3", {"start": v(37.1, 15.56) * mm, "mid": v(36.83, 15.89) * mm, "end": v(36.44, 16.05) * mm});
            skLineSegment(sketch, "E13.29.4", {"start": v(37.1, 15.56) * mm, "end": v(37.16, 15.4) * mm});
            skLineSegment(sketch, "E13.29.5", {"start": v(37.23, 15.23) * mm, "end": v(37.16, 15.4) * mm});
            skArc(sketch, "E13.29.6", {"start": v(37.12, 14.42) * mm, "mid": v(37.28, 14.8) * mm, "end": v(37.23, 15.23) * mm});
            skArc(sketch, "E13.29.7", {"start": v(35.93, 13.13) * mm, "mid": v(36.55, 13.75) * mm, "end": v(37.12, 14.42) * mm});
            skLineSegment(sketch, "E13.29.8", {"start": v(35.66, 12.97) * mm, "end": v(34.58, 12.58) * mm});
            skArc(sketch, "E13.29.9", {"start": v(34.58, 12.58) * mm, "mid": v(34.12, 12.16) * mm, "end": v(34.08, 11.54) * mm});
            skArc(sketch, "E13.29.10", {"start": v(35.66, 12.97) * mm, "mid": v(35.8, 13.04) * mm, "end": v(35.93, 13.13) * mm});
            skPoint(sketch, "E13.29.11", {"position": v(34.53, 16.1) * mm});
            skArc(sketch, "E13.29.12", {"start": v(34.7, 16.12) * mm, "mid": v(34.53, 16.1) * mm, "end": v(34.38, 16.04) * mm});
            skArc(sketch, "E13.30.0", {"start": v(29, 21.3) * mm, "mid": v(29.53, 20.98) * mm, "end": v(30.14, 21.11) * mm});
            skLineSegment(sketch, "E13.30.1", {"start": v(31.08, 21.77) * mm, "end": v(30.14, 21.11) * mm});
            skArc(sketch, "E13.30.2", {"start": v(31.36, 21.9) * mm, "mid": v(32.23, 22.06) * mm, "end": v(33.1, 22.13) * mm});
            skArc(sketch, "E13.30.3", {"start": v(33.83, 21.76) * mm, "mid": v(33.51, 22.04) * mm, "end": v(33.1, 22.13) * mm});
            skLineSegment(sketch, "E13.30.4", {"start": v(33.83, 21.76) * mm, "end": v(33.93, 21.61) * mm});
            skLineSegment(sketch, "E13.30.5", {"start": v(34.02, 21.46) * mm, "end": v(33.93, 21.61) * mm});
            skArc(sketch, "E13.30.6", {"start": v(34.05, 20.65) * mm, "mid": v(34.14, 21.06) * mm, "end": v(34.02, 21.46) * mm});
            skArc(sketch, "E13.30.7", {"start": v(33.1, 19.17) * mm, "mid": v(33.61, 19.89) * mm, "end": v(34.05, 20.65) * mm});
            skLineSegment(sketch, "E13.30.8", {"start": v(32.86, 18.96) * mm, "end": v(31.87, 18.4) * mm});
            skArc(sketch, "E13.30.9", {"start": v(31.87, 18.4) * mm, "mid": v(31.5, 17.9) * mm, "end": v(31.56, 17.28) * mm});
            skArc(sketch, "E13.30.10", {"start": v(32.86, 18.96) * mm, "mid": v(33, 19.06) * mm, "end": v(33.1, 19.17) * mm});
            skPoint(sketch, "E13.30.11", {"position": v(31.2, 21.86) * mm});
            skArc(sketch, "E13.30.12", {"start": v(31.36, 21.9) * mm, "mid": v(31.21, 21.85) * mm, "end": v(31.08, 21.77) * mm});
            skArc(sketch, "E13.31.0", {"start": v(24.86, 26.01) * mm, "mid": v(25.44, 25.79) * mm, "end": v(26.01, 26.03) * mm});
            skLineSegment(sketch, "E13.31.1", {"start": v(26.82, 26.84) * mm, "end": v(26.01, 26.03) * mm});
            skArc(sketch, "E13.31.2", {"start": v(27.09, 27.01) * mm, "mid": v(27.9, 27.32) * mm, "end": v(28.76, 27.55) * mm});
            skArc(sketch, "E13.31.3", {"start": v(29.53, 27.3) * mm, "mid": v(29.18, 27.53) * mm, "end": v(28.76, 27.55) * mm});
            skLineSegment(sketch, "E13.31.4", {"start": v(29.53, 27.3) * mm, "end": v(29.66, 27.18) * mm});
            skLineSegment(sketch, "E13.31.5", {"start": v(29.78, 27.04) * mm, "end": v(29.66, 27.18) * mm});
            skArc(sketch, "E13.31.6", {"start": v(29.95, 26.25) * mm, "mid": v(29.97, 26.67) * mm, "end": v(29.78, 27.04) * mm});
            skArc(sketch, "E13.31.7", {"start": v(29.27, 24.63) * mm, "mid": v(29.65, 25.42) * mm, "end": v(29.95, 26.25) * mm});
            skLineSegment(sketch, "E13.31.8", {"start": v(29.07, 24.38) * mm, "end": v(28.2, 23.65) * mm});
            skArc(sketch, "E13.31.9", {"start": v(28.2, 23.65) * mm, "mid": v(27.9, 23.1) * mm, "end": v(28.08, 22.5) * mm});
            skArc(sketch, "E13.31.10", {"start": v(29.07, 24.38) * mm, "mid": v(29.18, 24.5) * mm, "end": v(29.27, 24.63) * mm});
            skPoint(sketch, "E13.31.11", {"position": v(26.93, 26.95) * mm});
            skArc(sketch, "E13.31.12", {"start": v(27.09, 27.01) * mm, "mid": v(26.95, 26.94) * mm, "end": v(26.82, 26.84) * mm});
            skArc(sketch, "E13.32.0", {"start": v(19.97, 29.94) * mm, "mid": v(20.58, 29.81) * mm, "end": v(21.1, 30.15) * mm});
            skLineSegment(sketch, "E13.32.1", {"start": v(21.76, 31.09) * mm, "end": v(21.1, 30.15) * mm});
            skArc(sketch, "E13.32.2", {"start": v(21.98, 31.3) * mm, "mid": v(22.74, 31.75) * mm, "end": v(23.54, 32.12) * mm});
            skArc(sketch, "E13.32.3", {"start": v(24.34, 32.02) * mm, "mid": v(23.95, 32.18) * mm, "end": v(23.54, 32.12) * mm});
            skLineSegment(sketch, "E13.32.4", {"start": v(24.34, 32.02) * mm, "end": v(24.49, 31.91) * mm});
            skLineSegment(sketch, "E13.32.5", {"start": v(24.63, 31.8) * mm, "end": v(24.49, 31.91) * mm});
            skArc(sketch, "E13.32.6", {"start": v(24.93, 31.05) * mm, "mid": v(24.88, 31.47) * mm, "end": v(24.63, 31.8) * mm});
            skArc(sketch, "E13.32.7", {"start": v(24.55, 29.34) * mm, "mid": v(24.78, 30.18) * mm, "end": v(24.93, 31.05) * mm});
            skLineSegment(sketch, "E13.32.8", {"start": v(24.4, 29.06) * mm, "end": v(23.66, 28.18) * mm});
            skArc(sketch, "E13.32.9", {"start": v(23.66, 28.18) * mm, "mid": v(23.47, 27.6) * mm, "end": v(23.75, 27.03) * mm});
            skArc(sketch, "E13.32.10", {"start": v(24.4, 29.06) * mm, "mid": v(24.49, 29.2) * mm, "end": v(24.55, 29.34) * mm});
            skPoint(sketch, "E13.32.11", {"position": v(21.85, 31.21) * mm});
            skArc(sketch, "E13.32.12", {"start": v(21.98, 31.3) * mm, "mid": v(21.86, 31.2) * mm, "end": v(21.76, 31.09) * mm});
            skArc(sketch, "E13.33.0", {"start": v(14.46, 32.95) * mm, "mid": v(15.09, 32.93) * mm, "end": v(15.54, 33.36) * mm});
            skLineSegment(sketch, "E13.33.1", {"start": v(16.03, 34.4) * mm, "end": v(15.54, 33.36) * mm});
            skArc(sketch, "E13.33.2", {"start": v(16.21, 34.65) * mm, "mid": v(16.88, 35.22) * mm, "end": v(17.6, 35.72) * mm});
            skArc(sketch, "E13.33.3", {"start": v(18.41, 35.76) * mm, "mid": v(18, 35.85) * mm, "end": v(17.6, 35.72) * mm});
            skLineSegment(sketch, "E13.33.4", {"start": v(18.41, 35.76) * mm, "end": v(18.57, 35.68) * mm});
            skLineSegment(sketch, "E13.33.5", {"start": v(18.73, 35.6) * mm, "end": v(18.57, 35.68) * mm});
            skArc(sketch, "E13.33.6", {"start": v(19.16, 34.9) * mm, "mid": v(19.04, 35.3) * mm, "end": v(18.73, 35.6) * mm});
            skArc(sketch, "E13.33.7", {"start": v(19.08, 33.15) * mm, "mid": v(19.16, 34.03) * mm, "end": v(19.16, 34.9) * mm});
            skLineSegment(sketch, "E13.33.8", {"start": v(18.98, 32.86) * mm, "end": v(18.4, 31.86) * mm});
            skArc(sketch, "E13.33.9", {"start": v(18.4, 31.86) * mm, "mid": v(18.32, 31.25) * mm, "end": v(18.7, 30.75) * mm});
            skArc(sketch, "E13.33.10", {"start": v(18.98, 32.86) * mm, "mid": v(19.04, 33) * mm, "end": v(19.08, 33.15) * mm});
            skPoint(sketch, "E13.33.11", {"position": v(16.1, 34.53) * mm});
            skArc(sketch, "E13.33.12", {"start": v(16.21, 34.65) * mm, "mid": v(16.1, 34.53) * mm, "end": v(16.03, 34.4) * mm});
            skArc(sketch, "E13.34.0", {"start": v(8.52, 34.96) * mm, "mid": v(9.14, 35.05) * mm, "end": v(9.52, 35.55) * mm});
            skLineSegment(sketch, "E13.34.1", {"start": v(9.81, 36.65) * mm, "end": v(9.52, 35.55) * mm});
            skArc(sketch, "E13.34.2", {"start": v(9.95, 36.94) * mm, "mid": v(10.51, 37.61) * mm, "end": v(11.13, 38.23) * mm});
            skArc(sketch, "E13.34.3", {"start": v(11.92, 38.42) * mm, "mid": v(11.5, 38.43) * mm, "end": v(11.13, 38.23) * mm});
            skLineSegment(sketch, "E13.34.4", {"start": v(11.92, 38.42) * mm, "end": v(12.1, 38.36) * mm});
            skLineSegment(sketch, "E13.34.5", {"start": v(12.27, 38.3) * mm, "end": v(12.1, 38.36) * mm});
            skArc(sketch, "E13.34.6", {"start": v(12.81, 37.7) * mm, "mid": v(12.62, 38.08) * mm, "end": v(12.27, 38.3) * mm});
            skArc(sketch, "E13.34.7", {"start": v(13.03, 35.96) * mm, "mid": v(12.96, 36.84) * mm, "end": v(12.81, 37.7) * mm});
            skLineSegment(sketch, "E13.34.8", {"start": v(12.99, 35.65) * mm, "end": v(12.6, 34.58) * mm});
            skArc(sketch, "E13.34.9", {"start": v(12.6, 34.58) * mm, "mid": v(12.62, 33.95) * mm, "end": v(13.07, 33.53) * mm});
            skArc(sketch, "E13.34.10", {"start": v(12.99, 35.65) * mm, "mid": v(13.03, 35.8) * mm, "end": v(13.03, 35.96) * mm});
            skPoint(sketch, "E13.34.11", {"position": v(9.85, 36.8) * mm});
            skArc(sketch, "E13.34.12", {"start": v(9.95, 36.94) * mm, "mid": v(9.87, 36.8) * mm, "end": v(9.81, 36.65) * mm});
            skArc(sketch, "E13.35.0", {"start": v(2.32, 35.9) * mm, "mid": v(2.91, 36.1) * mm, "end": v(3.2, 36.66) * mm});
            skLineSegment(sketch, "E13.35.1", {"start": v(3.3, 37.8) * mm, "end": v(3.2, 36.66) * mm});
            skArc(sketch, "E13.35.2", {"start": v(3.39, 38.1) * mm, "mid": v(3.82, 38.87) * mm, "end": v(4.32, 39.59) * mm});
            skArc(sketch, "E13.35.3", {"start": v(5.07, 39.9) * mm, "mid": v(4.66, 39.84) * mm, "end": v(4.32, 39.59) * mm});
            skLineSegment(sketch, "E13.35.4", {"start": v(5.07, 39.9) * mm, "end": v(5.25, 39.88) * mm});
            skLineSegment(sketch, "E13.35.5", {"start": v(5.43, 39.86) * mm, "end": v(5.25, 39.88) * mm});
            skArc(sketch, "E13.35.6", {"start": v(6.07, 39.36) * mm, "mid": v(5.82, 39.7) * mm, "end": v(5.43, 39.86) * mm});
            skArc(sketch, "E13.35.7", {"start": v(6.6, 37.68) * mm, "mid": v(6.37, 38.53) * mm, "end": v(6.07, 39.36) * mm});
            skLineSegment(sketch, "E13.35.8", {"start": v(6.6, 37.37) * mm, "end": v(6.4, 36.24) * mm});
            skArc(sketch, "E13.35.9", {"start": v(6.4, 36.24) * mm, "mid": v(6.53, 35.63) * mm, "end": v(7.05, 35.29) * mm});
            skArc(sketch, "E13.35.10", {"start": v(6.6, 37.37) * mm, "mid": v(6.6, 37.52) * mm, "end": v(6.6, 37.68) * mm});
            skPoint(sketch, "E13.35.11", {"position": v(3.31, 37.96) * mm});
            skArc(sketch, "E13.35.12", {"start": v(3.39, 38.1) * mm, "mid": v(3.33, 37.96) * mm, "end": v(3.3, 37.8) * mm});
            skArc(sketch, "E14.trimOffspring", {"start": v(19.97, 29.94) * mm, "mid": v(19.33, 30.35) * mm, "end": v(18.7, 30.75) * mm});
            skArc(sketch, "E15.trimOffspring", {"start": v(14.46, 32.95) * mm, "mid": v(13.77, 33.24) * mm, "end": v(13.07, 33.53) * mm});
            skArc(sketch, "E16.trimOffspring", {"start": v(8.52, 34.96) * mm, "mid": v(7.79, 35.13) * mm, "end": v(7.05, 35.29) * mm});
            skArc(sketch, "E17.trimOffspring", {"start": v(2.32, 35.9) * mm, "mid": v(1.57, 35.95) * mm, "end": v(0.82, 35.97) * mm});
            skArc(sketch, "E18.trimOffspring", {"start": v(24.86, 26.01) * mm, "mid": v(24.3, 26.53) * mm, "end": v(23.75, 27.03) * mm});
            skArc(sketch, "E19.trimOffspring", {"start": v(29, 21.3) * mm, "mid": v(28.55, 21.9) * mm, "end": v(28.08, 22.5) * mm});
            skArc(sketch, "E20.trimOffspring", {"start": v(32.26, 15.94) * mm, "mid": v(31.92, 16.62) * mm, "end": v(31.56, 17.28) * mm});
            skArc(sketch, "E21.trimOffspring", {"start": v(34.54, 10.1) * mm, "mid": v(34.32, 10.82) * mm, "end": v(34.08, 11.54) * mm});
            skArc(sketch, "E22.trimOffspring", {"start": v(35.77, 3.95) * mm, "mid": v(35.68, 4.7) * mm, "end": v(35.57, 5.44) * mm});
            skArc(sketch, "E23.trimOffspring", {"start": v(35.9, -2.32) * mm, "mid": v(35.95, -1.57) * mm, "end": v(35.97, -0.82) * mm});
            skArc(sketch, "E24.trimOffspring", {"start": v(34.96, -8.52) * mm, "mid": v(35.13, -7.79) * mm, "end": v(35.29, -7.05) * mm});
            skArc(sketch, "E25.trimOffspring", {"start": v(32.95, -14.46) * mm, "mid": v(33.24, -13.77) * mm, "end": v(33.53, -13.07) * mm});
            skArc(sketch, "E26.trimOffspring", {"start": v(29.94, -19.97) * mm, "mid": v(30.35, -19.33) * mm, "end": v(30.75, -18.7) * mm});
            skArc(sketch, "E27.trimOffspring", {"start": v(26.01, -24.86) * mm, "mid": v(26.53, -24.3) * mm, "end": v(27.03, -23.75) * mm});
            skArc(sketch, "E28.trimOffspring", {"start": v(21.3, -29) * mm, "mid": v(21.9, -28.55) * mm, "end": v(22.5, -28.08) * mm});
            skArc(sketch, "E29.trimOffspring", {"start": v(15.94, -32.26) * mm, "mid": v(16.62, -31.92) * mm, "end": v(17.28, -31.56) * mm});
            skArc(sketch, "E30.trimOffspring", {"start": v(10.1, -34.54) * mm, "mid": v(10.82, -34.32) * mm, "end": v(11.54, -34.08) * mm});
            skArc(sketch, "E31.trimOffspring", {"start": v(3.95, -35.77) * mm, "mid": v(4.7, -35.68) * mm, "end": v(5.44, -35.57) * mm});
            skArc(sketch, "E32.trimOffspring", {"start": v(-2.32, -35.9) * mm, "mid": v(-1.57, -35.95) * mm, "end": v(-0.82, -35.97) * mm});
            skArc(sketch, "E33.trimOffspring", {"start": v(-8.52, -34.96) * mm, "mid": v(-7.79, -35.13) * mm, "end": v(-7.05, -35.29) * mm});
            skArc(sketch, "E34.trimOffspring", {"start": v(-14.46, -32.95) * mm, "mid": v(-13.77, -33.24) * mm, "end": v(-13.07, -33.53) * mm});
            skArc(sketch, "E35.trimOffspring", {"start": v(-19.97, -29.94) * mm, "mid": v(-19.33, -30.35) * mm, "end": v(-18.7, -30.75) * mm});
            skArc(sketch, "E36.trimOffspring", {"start": v(-24.86, -26.01) * mm, "mid": v(-24.3, -26.53) * mm, "end": v(-23.75, -27.03) * mm});
            skArc(sketch, "E37.trimOffspring", {"start": v(-29, -21.3) * mm, "mid": v(-28.55, -21.9) * mm, "end": v(-28.08, -22.5) * mm});
            skArc(sketch, "E38.trimOffspring", {"start": v(-32.26, -15.94) * mm, "mid": v(-31.92, -16.62) * mm, "end": v(-31.56, -17.28) * mm});
            skArc(sketch, "E39.trimOffspring", {"start": v(-34.54, -10.1) * mm, "mid": v(-34.32, -10.82) * mm, "end": v(-34.08, -11.54) * mm});
            skArc(sketch, "E40.trimOffspring", {"start": v(-35.77, -3.95) * mm, "mid": v(-35.68, -4.7) * mm, "end": v(-35.57, -5.44) * mm});
            skArc(sketch, "E41.trimOffspring", {"start": v(-35.9, 2.32) * mm, "mid": v(-35.95, 1.57) * mm, "end": v(-35.97, 0.82) * mm});
            skArc(sketch, "E42.trimOffspring", {"start": v(-34.96, 8.52) * mm, "mid": v(-35.13, 7.79) * mm, "end": v(-35.29, 7.05) * mm});
            skArc(sketch, "E43.trimOffspring", {"start": v(-32.95, 14.46) * mm, "mid": v(-33.24, 13.77) * mm, "end": v(-33.53, 13.07) * mm});
            skArc(sketch, "E44.trimOffspring", {"start": v(-29.94, 19.97) * mm, "mid": v(-30.35, 19.33) * mm, "end": v(-30.75, 18.7) * mm});
            skArc(sketch, "E45.trimOffspring", {"start": v(-26.01, 24.86) * mm, "mid": v(-26.53, 24.3) * mm, "end": v(-27.03, 23.75) * mm});
            skArc(sketch, "E46.trimOffspring", {"start": v(-21.3, 29) * mm, "mid": v(-21.9, 28.55) * mm, "end": v(-22.5, 28.08) * mm});
            skArc(sketch, "E47.trimOffspring", {"start": v(-15.94, 32.26) * mm, "mid": v(-16.62, 31.92) * mm, "end": v(-17.28, 31.56) * mm});
            skArc(sketch, "E48.trimOffspring", {"start": v(-10.1, 34.54) * mm, "mid": v(-10.82, 34.32) * mm, "end": v(-11.54, 34.08) * mm});
            skSolve(sketch);
        }
        {
            var Q0;
            Q0 = qSketchRegion(id + "F1", true);
            extrude(context, id + "F2", {"entities" : qUnion([Q0]), "depth" : 12.7 * mm});
        }
        {
            var Q0;
            Q0=makeQuery(id+"F2.opExtrude","CAP_FACE",FACE,{"disambiguationData":[OSD([sQuery(id+"F1.wireOp",EDGE,"E0"),sQuery(id+"F1.wireOp",EDGE,"E1.trimOffspring"),sQuery(id+"F1.wireOp",EDGE,"E2"),sQuery(id+"F1.wireOp",EDGE,"E3"),sQuery(id+"F1.wireOp",EDGE,"E4.MirrorCS"),sQuery(id+"F1.wireOp",EDGE,"E5.MirrorCS"),sQuery(id+"F1.wireOp",EDGE,"E6.MirrorCS"),sQuery(id+"F1.wireOp",EDGE,"E7.filletArc"),sQuery(id+"F1.wireOp",EDGE,"E8.filletArc"),sQuery(id+"F1.wireOp",EDGE,"E9.filletArc"),sQuery(id+"F1.wireOp",EDGE,"E10.filletArc"),sQuery(id+"F1.wireOp",EDGE,"E11.filletArc"),sQuery(id+"F1.wireOp",EDGE,"E12.filletArc"),sQuery(id+"F1.wireOp",EDGE,"E13.1.0"),sQuery(id+"F1.wireOp",EDGE,"E13.1.1"),sQuery(id+"F1.wireOp",EDGE,"E13.1.2"),sQuery(id+"F1.wireOp",EDGE,"E13.1.3"),sQuery(id+"F1.wireOp",EDGE,"E13.1.4"),sQuery(id+"F1.wireOp",EDGE,"E13.1.5"),sQuery(id+"F1.wireOp",EDGE,"E13.1.6"),sQuery(id+"F1.wireOp",EDGE,"E13.1.7"),sQuery(id+"F1.wireOp",EDGE,"E13.1.8"),sQuery(id+"F1.wireOp",EDGE,"E13.1.9"),sQuery(id+"F1.wireOp",EDGE,"E13.1.10"),sQuery(id+"F1.wireOp",EDGE,"E13.1.12"),sQuery(id+"F1.wireOp",EDGE,"E13.2.0"),sQuery(id+"F1.wireOp",EDGE,"E13.2.1"),sQuery(id+"F1.wireOp",EDGE,"E13.2.2"),sQuery(id+"F1.wireOp",EDGE,"E13.2.3"),sQuery(id+"F1.wireOp",EDGE,"E13.2.4"),sQuery(id+"F1.wireOp",EDGE,"E13.2.5"),sQuery(id+"F1.wireOp",EDGE,"E13.2.6"),sQuery(id+"F1.wireOp",EDGE,"E13.2.7"),sQuery(id+"F1.wireOp",EDGE,"E13.2.8"),sQuery(id+"F1.wireOp",EDGE,"E13.2.9"),sQuery(id+"F1.wireOp",EDGE,"E13.2.10"),sQuery(id+"F1.wireOp",EDGE,"E13.2.12"),sQuery(id+"F1.wireOp",EDGE,"E13.3.0"),sQuery(id+"F1.wireOp",EDGE,"E13.3.1"),sQuery(id+"F1.wireOp",EDGE,"E13.3.2"),sQuery(id+"F1.wireOp",EDGE,"E13.3.3"),sQuery(id+"F1.wireOp",EDGE,"E13.3.4"),sQuery(id+"F1.wireOp",EDGE,"E13.3.5"),sQuery(id+"F1.wireOp",EDGE,"E13.3.6"),sQuery(id+"F1.wireOp",EDGE,"E13.3.7"),sQuery(id+"F1.wireOp",EDGE,"E13.3.8"),sQuery(id+"F1.wireOp",EDGE,"E13.3.9"),sQuery(id+"F1.wireOp",EDGE,"E13.3.10"),sQuery(id+"F1.wireOp",EDGE,"E13.3.12"),sQuery(id+"F1.wireOp",EDGE,"E13.4.0"),sQuery(id+"F1.wireOp",EDGE,"E13.4.1"),sQuery(id+"F1.wireOp",EDGE,"E13.4.2"),sQuery(id+"F1.wireOp",EDGE,"E13.4.3"),sQuery(id+"F1.wireOp",EDGE,"E13.4.4"),sQuery(id+"F1.wireOp",EDGE,"E13.4.5"),sQuery(id+"F1.wireOp",EDGE,"E13.4.6"),sQuery(id+"F1.wireOp",EDGE,"E13.4.7"),sQuery(id+"F1.wireOp",EDGE,"E13.4.8"),sQuery(id+"F1.wireOp",EDGE,"E13.4.9"),sQuery(id+"F1.wireOp",EDGE,"E13.4.10"),sQuery(id+"F1.wireOp",EDGE,"E13.4.12"),sQuery(id+"F1.wireOp",EDGE,"E13.5.0"),sQuery(id+"F1.wireOp",EDGE,"E13.5.1"),sQuery(id+"F1.wireOp",EDGE,"E13.5.2"),sQuery(id+"F1.wireOp",EDGE,"E13.5.3"),sQuery(id+"F1.wireOp",EDGE,"E13.5.4"),sQuery(id+"F1.wireOp",EDGE,"E13.5.5"),sQuery(id+"F1.wireOp",EDGE,"E13.5.6"),sQuery(id+"F1.wireOp",EDGE,"E13.5.7"),sQuery(id+"F1.wireOp",EDGE,"E13.5.8"),sQuery(id+"F1.wireOp",EDGE,"E13.5.9"),sQuery(id+"F1.wireOp",EDGE,"E13.5.10"),sQuery(id+"F1.wireOp",EDGE,"E13.5.12"),sQuery(id+"F1.wireOp",EDGE,"E13.6.0"),sQuery(id+"F1.wireOp",EDGE,"E13.6.1"),sQuery(id+"F1.wireOp",EDGE,"E13.6.2"),sQuery(id+"F1.wireOp",EDGE,"E13.6.3"),sQuery(id+"F1.wireOp",EDGE,"E13.6.4"),sQuery(id+"F1.wireOp",EDGE,"E13.6.5"),sQuery(id+"F1.wireOp",EDGE,"E13.6.6"),sQuery(id+"F1.wireOp",EDGE,"E13.6.7"),sQuery(id+"F1.wireOp",EDGE,"E13.6.8"),sQuery(id+"F1.wireOp",EDGE,"E13.6.9"),sQuery(id+"F1.wireOp",EDGE,"E13.6.10"),sQuery(id+"F1.wireOp",EDGE,"E13.6.12"),sQuery(id+"F1.wireOp",EDGE,"E13.7.0"),sQuery(id+"F1.wireOp",EDGE,"E13.7.1"),sQuery(id+"F1.wireOp",EDGE,"E13.7.2"),sQuery(id+"F1.wireOp",EDGE,"E13.7.3"),sQuery(id+"F1.wireOp",EDGE,"E13.7.4"),sQuery(id+"F1.wireOp",EDGE,"E13.7.5"),sQuery(id+"F1.wireOp",EDGE,"E13.7.6"),sQuery(id+"F1.wireOp",EDGE,"E13.7.7"),sQuery(id+"F1.wireOp",EDGE,"E13.7.8"),sQuery(id+"F1.wireOp",EDGE,"E13.7.9"),sQuery(id+"F1.wireOp",EDGE,"E13.7.10"),sQuery(id+"F1.wireOp",EDGE,"E13.7.12"),sQuery(id+"F1.wireOp",EDGE,"E13.8.0"),sQuery(id+"F1.wireOp",EDGE,"E13.8.1"),sQuery(id+"F1.wireOp",EDGE,"E13.8.2"),sQuery(id+"F1.wireOp",EDGE,"E13.8.3"),sQuery(id+"F1.wireOp",EDGE,"E13.8.4"),sQuery(id+"F1.wireOp",EDGE,"E13.8.5"),sQuery(id+"F1.wireOp",EDGE,"E13.8.6"),sQuery(id+"F1.wireOp",EDGE,"E13.8.7"),sQuery(id+"F1.wireOp",EDGE,"E13.8.8"),sQuery(id+"F1.wireOp",EDGE,"E13.8.9"),sQuery(id+"F1.wireOp",EDGE,"E13.8.10"),sQuery(id+"F1.wireOp",EDGE,"E13.8.12"),sQuery(id+"F1.wireOp",EDGE,"E13.9.0"),sQuery(id+"F1.wireOp",EDGE,"E13.9.1"),sQuery(id+"F1.wireOp",EDGE,"E13.9.2"),sQuery(id+"F1.wireOp",EDGE,"E13.9.3"),sQuery(id+"F1.wireOp",EDGE,"E13.9.4"),sQuery(id+"F1.wireOp",EDGE,"E13.9.5"),sQuery(id+"F1.wireOp",EDGE,"E13.9.6"),sQuery(id+"F1.wireOp",EDGE,"E13.9.7"),sQuery(id+"F1.wireOp",EDGE,"E13.9.8"),sQuery(id+"F1.wireOp",EDGE,"E13.9.9"),sQuery(id+"F1.wireOp",EDGE,"E13.9.10"),sQuery(id+"F1.wireOp",EDGE,"E13.9.12"),sQuery(id+"F1.wireOp",EDGE,"E13.10.0"),sQuery(id+"F1.wireOp",EDGE,"E13.10.1"),sQuery(id+"F1.wireOp",EDGE,"E13.10.2"),sQuery(id+"F1.wireOp",EDGE,"E13.10.3"),sQuery(id+"F1.wireOp",EDGE,"E13.10.4"),sQuery(id+"F1.wireOp",EDGE,"E13.10.5"),sQuery(id+"F1.wireOp",EDGE,"E13.10.6"),sQuery(id+"F1.wireOp",EDGE,"E13.10.7"),sQuery(id+"F1.wireOp",EDGE,"E13.10.8"),sQuery(id+"F1.wireOp",EDGE,"E13.10.9"),sQuery(id+"F1.wireOp",EDGE,"E13.10.10"),sQuery(id+"F1.wireOp",EDGE,"E13.10.12"),sQuery(id+"F1.wireOp",EDGE,"E13.11.0"),sQuery(id+"F1.wireOp",EDGE,"E13.11.1"),sQuery(id+"F1.wireOp",EDGE,"E13.11.2"),sQuery(id+"F1.wireOp",EDGE,"E13.11.3"),sQuery(id+"F1.wireOp",EDGE,"E13.11.4"),sQuery(id+"F1.wireOp",EDGE,"E13.11.5"),sQuery(id+"F1.wireOp",EDGE,"E13.11.6"),sQuery(id+"F1.wireOp",EDGE,"E13.11.7"),sQuery(id+"F1.wireOp",EDGE,"E13.11.8"),sQuery(id+"F1.wireOp",EDGE,"E13.11.9"),sQuery(id+"F1.wireOp",EDGE,"E13.11.10"),sQuery(id+"F1.wireOp",EDGE,"E13.11.12"),sQuery(id+"F1.wireOp",EDGE,"E13.12.0"),sQuery(id+"F1.wireOp",EDGE,"E13.12.1"),sQuery(id+"F1.wireOp",EDGE,"E13.12.2"),sQuery(id+"F1.wireOp",EDGE,"E13.12.3"),sQuery(id+"F1.wireOp",EDGE,"E13.12.4"),sQuery(id+"F1.wireOp",EDGE,"E13.12.5"),sQuery(id+"F1.wireOp",EDGE,"E13.12.6"),sQuery(id+"F1.wireOp",EDGE,"E13.12.7"),sQuery(id+"F1.wireOp",EDGE,"E13.12.8"),sQuery(id+"F1.wireOp",EDGE,"E13.12.9"),sQuery(id+"F1.wireOp",EDGE,"E13.12.10"),sQuery(id+"F1.wireOp",EDGE,"E13.12.12"),sQuery(id+"F1.wireOp",EDGE,"E13.13.0"),sQuery(id+"F1.wireOp",EDGE,"E13.13.1"),sQuery(id+"F1.wireOp",EDGE,"E13.13.2"),sQuery(id+"F1.wireOp",EDGE,"E13.13.3"),sQuery(id+"F1.wireOp",EDGE,"E13.13.4"),sQuery(id+"F1.wireOp",EDGE,"E13.13.5"),sQuery(id+"F1.wireOp",EDGE,"E13.13.6"),sQuery(id+"F1.wireOp",EDGE,"E13.13.7"),sQuery(id+"F1.wireOp",EDGE,"E13.13.8"),sQuery(id+"F1.wireOp",EDGE,"E13.13.9"),sQuery(id+"F1.wireOp",EDGE,"E13.13.10"),sQuery(id+"F1.wireOp",EDGE,"E13.13.12"),sQuery(id+"F1.wireOp",EDGE,"E13.14.0"),sQuery(id+"F1.wireOp",EDGE,"E13.14.1"),sQuery(id+"F1.wireOp",EDGE,"E13.14.2"),sQuery(id+"F1.wireOp",EDGE,"E13.14.3"),sQuery(id+"F1.wireOp",EDGE,"E13.14.4"),sQuery(id+"F1.wireOp",EDGE,"E13.14.5"),sQuery(id+"F1.wireOp",EDGE,"E13.14.6"),sQuery(id+"F1.wireOp",EDGE,"E13.14.7"),sQuery(id+"F1.wireOp",EDGE,"E13.14.8"),sQuery(id+"F1.wireOp",EDGE,"E13.14.9"),sQuery(id+"F1.wireOp",EDGE,"E13.14.10"),sQuery(id+"F1.wireOp",EDGE,"E13.14.12"),sQuery(id+"F1.wireOp",EDGE,"E13.15.0"),sQuery(id+"F1.wireOp",EDGE,"E13.15.1"),sQuery(id+"F1.wireOp",EDGE,"E13.15.2"),sQuery(id+"F1.wireOp",EDGE,"E13.15.3"),sQuery(id+"F1.wireOp",EDGE,"E13.15.4"),sQuery(id+"F1.wireOp",EDGE,"E13.15.5"),sQuery(id+"F1.wireOp",EDGE,"E13.15.6"),sQuery(id+"F1.wireOp",EDGE,"E13.15.7"),sQuery(id+"F1.wireOp",EDGE,"E13.15.8"),sQuery(id+"F1.wireOp",EDGE,"E13.15.9"),sQuery(id+"F1.wireOp",EDGE,"E13.15.10"),sQuery(id+"F1.wireOp",EDGE,"E13.15.12"),sQuery(id+"F1.wireOp",EDGE,"E13.16.0"),sQuery(id+"F1.wireOp",EDGE,"E13.16.1"),sQuery(id+"F1.wireOp",EDGE,"E13.16.2"),sQuery(id+"F1.wireOp",EDGE,"E13.16.3"),sQuery(id+"F1.wireOp",EDGE,"E13.16.4"),sQuery(id+"F1.wireOp",EDGE,"E13.16.5"),sQuery(id+"F1.wireOp",EDGE,"E13.16.6"),sQuery(id+"F1.wireOp",EDGE,"E13.16.7"),sQuery(id+"F1.wireOp",EDGE,"E13.16.8"),sQuery(id+"F1.wireOp",EDGE,"E13.16.9"),sQuery(id+"F1.wireOp",EDGE,"E13.16.10"),sQuery(id+"F1.wireOp",EDGE,"E13.16.12"),sQuery(id+"F1.wireOp",EDGE,"E13.17.0"),sQuery(id+"F1.wireOp",EDGE,"E13.17.1"),sQuery(id+"F1.wireOp",EDGE,"E13.17.2"),sQuery(id+"F1.wireOp",EDGE,"E13.17.3"),sQuery(id+"F1.wireOp",EDGE,"E13.17.4"),sQuery(id+"F1.wireOp",EDGE,"E13.17.5"),sQuery(id+"F1.wireOp",EDGE,"E13.17.6"),sQuery(id+"F1.wireOp",EDGE,"E13.17.7"),sQuery(id+"F1.wireOp",EDGE,"E13.17.8"),sQuery(id+"F1.wireOp",EDGE,"E13.17.9"),sQuery(id+"F1.wireOp",EDGE,"E13.17.10"),sQuery(id+"F1.wireOp",EDGE,"E13.17.12"),sQuery(id+"F1.wireOp",EDGE,"E13.18.0"),sQuery(id+"F1.wireOp",EDGE,"E13.18.1"),sQuery(id+"F1.wireOp",EDGE,"E13.18.2"),sQuery(id+"F1.wireOp",EDGE,"E13.18.3"),sQuery(id+"F1.wireOp",EDGE,"E13.18.4"),sQuery(id+"F1.wireOp",EDGE,"E13.18.5"),sQuery(id+"F1.wireOp",EDGE,"E13.18.6"),sQuery(id+"F1.wireOp",EDGE,"E13.18.7"),sQuery(id+"F1.wireOp",EDGE,"E13.18.8"),sQuery(id+"F1.wireOp",EDGE,"E13.18.9"),sQuery(id+"F1.wireOp",EDGE,"E13.18.10"),sQuery(id+"F1.wireOp",EDGE,"E13.18.12"),sQuery(id+"F1.wireOp",EDGE,"E13.19.0"),sQuery(id+"F1.wireOp",EDGE,"E13.19.1"),sQuery(id+"F1.wireOp",EDGE,"E13.19.2"),sQuery(id+"F1.wireOp",EDGE,"E13.19.3"),sQuery(id+"F1.wireOp",EDGE,"E13.19.4"),sQuery(id+"F1.wireOp",EDGE,"E13.19.5"),sQuery(id+"F1.wireOp",EDGE,"E13.19.6"),sQuery(id+"F1.wireOp",EDGE,"E13.19.7"),sQuery(id+"F1.wireOp",EDGE,"E13.19.8"),sQuery(id+"F1.wireOp",EDGE,"E13.19.9"),sQuery(id+"F1.wireOp",EDGE,"E13.19.10"),sQuery(id+"F1.wireOp",EDGE,"E13.19.12"),sQuery(id+"F1.wireOp",EDGE,"E13.20.0"),sQuery(id+"F1.wireOp",EDGE,"E13.20.1"),sQuery(id+"F1.wireOp",EDGE,"E13.20.2"),sQuery(id+"F1.wireOp",EDGE,"E13.20.3"),sQuery(id+"F1.wireOp",EDGE,"E13.20.4"),sQuery(id+"F1.wireOp",EDGE,"E13.20.5"),sQuery(id+"F1.wireOp",EDGE,"E13.20.6"),sQuery(id+"F1.wireOp",EDGE,"E13.20.7"),sQuery(id+"F1.wireOp",EDGE,"E13.20.8"),sQuery(id+"F1.wireOp",EDGE,"E13.20.9"),sQuery(id+"F1.wireOp",EDGE,"E13.20.10"),sQuery(id+"F1.wireOp",EDGE,"E13.20.12"),sQuery(id+"F1.wireOp",EDGE,"E13.21.0"),sQuery(id+"F1.wireOp",EDGE,"E13.21.1"),sQuery(id+"F1.wireOp",EDGE,"E13.21.2"),sQuery(id+"F1.wireOp",EDGE,"E13.21.3"),sQuery(id+"F1.wireOp",EDGE,"E13.21.4"),sQuery(id+"F1.wireOp",EDGE,"E13.21.5"),sQuery(id+"F1.wireOp",EDGE,"E13.21.6"),sQuery(id+"F1.wireOp",EDGE,"E13.21.7"),sQuery(id+"F1.wireOp",EDGE,"E13.21.8"),sQuery(id+"F1.wireOp",EDGE,"E13.21.9"),sQuery(id+"F1.wireOp",EDGE,"E13.21.10"),sQuery(id+"F1.wireOp",EDGE,"E13.21.12"),sQuery(id+"F1.wireOp",EDGE,"E13.22.0"),sQuery(id+"F1.wireOp",EDGE,"E13.22.1"),sQuery(id+"F1.wireOp",EDGE,"E13.22.2"),sQuery(id+"F1.wireOp",EDGE,"E13.22.3"),sQuery(id+"F1.wireOp",EDGE,"E13.22.4"),sQuery(id+"F1.wireOp",EDGE,"E13.22.5"),sQuery(id+"F1.wireOp",EDGE,"E13.22.6"),sQuery(id+"F1.wireOp",EDGE,"E13.22.7"),sQuery(id+"F1.wireOp",EDGE,"E13.22.8"),sQuery(id+"F1.wireOp",EDGE,"E13.22.9"),sQuery(id+"F1.wireOp",EDGE,"E13.22.10"),sQuery(id+"F1.wireOp",EDGE,"E13.22.12"),sQuery(id+"F1.wireOp",EDGE,"E13.23.0"),sQuery(id+"F1.wireOp",EDGE,"E13.23.1"),sQuery(id+"F1.wireOp",EDGE,"E13.23.2"),sQuery(id+"F1.wireOp",EDGE,"E13.23.3"),sQuery(id+"F1.wireOp",EDGE,"E13.23.4"),sQuery(id+"F1.wireOp",EDGE,"E13.23.5"),sQuery(id+"F1.wireOp",EDGE,"E13.23.6"),sQuery(id+"F1.wireOp",EDGE,"E13.23.7"),sQuery(id+"F1.wireOp",EDGE,"E13.23.8"),sQuery(id+"F1.wireOp",EDGE,"E13.23.9"),sQuery(id+"F1.wireOp",EDGE,"E13.23.10"),sQuery(id+"F1.wireOp",EDGE,"E13.23.12"),sQuery(id+"F1.wireOp",EDGE,"E13.24.0"),sQuery(id+"F1.wireOp",EDGE,"E13.24.1"),sQuery(id+"F1.wireOp",EDGE,"E13.24.2"),sQuery(id+"F1.wireOp",EDGE,"E13.24.3"),sQuery(id+"F1.wireOp",EDGE,"E13.24.4"),sQuery(id+"F1.wireOp",EDGE,"E13.24.5"),sQuery(id+"F1.wireOp",EDGE,"E13.24.6"),sQuery(id+"F1.wireOp",EDGE,"E13.24.7"),sQuery(id+"F1.wireOp",EDGE,"E13.24.8"),sQuery(id+"F1.wireOp",EDGE,"E13.24.9"),sQuery(id+"F1.wireOp",EDGE,"E13.24.10"),sQuery(id+"F1.wireOp",EDGE,"E13.24.12"),sQuery(id+"F1.wireOp",EDGE,"E13.25.0"),sQuery(id+"F1.wireOp",EDGE,"E13.25.1"),sQuery(id+"F1.wireOp",EDGE,"E13.25.2"),sQuery(id+"F1.wireOp",EDGE,"E13.25.3"),sQuery(id+"F1.wireOp",EDGE,"E13.25.4"),sQuery(id+"F1.wireOp",EDGE,"E13.25.5"),sQuery(id+"F1.wireOp",EDGE,"E13.25.6"),sQuery(id+"F1.wireOp",EDGE,"E13.25.7"),sQuery(id+"F1.wireOp",EDGE,"E13.25.8"),sQuery(id+"F1.wireOp",EDGE,"E13.25.9"),sQuery(id+"F1.wireOp",EDGE,"E13.25.10"),sQuery(id+"F1.wireOp",EDGE,"E13.25.12"),sQuery(id+"F1.wireOp",EDGE,"E13.26.0"),sQuery(id+"F1.wireOp",EDGE,"E13.26.1"),sQuery(id+"F1.wireOp",EDGE,"E13.26.2"),sQuery(id+"F1.wireOp",EDGE,"E13.26.3"),sQuery(id+"F1.wireOp",EDGE,"E13.26.4"),sQuery(id+"F1.wireOp",EDGE,"E13.26.5"),sQuery(id+"F1.wireOp",EDGE,"E13.26.6"),sQuery(id+"F1.wireOp",EDGE,"E13.26.7"),sQuery(id+"F1.wireOp",EDGE,"E13.26.8"),sQuery(id+"F1.wireOp",EDGE,"E13.26.9"),sQuery(id+"F1.wireOp",EDGE,"E13.26.10"),sQuery(id+"F1.wireOp",EDGE,"E13.26.12"),sQuery(id+"F1.wireOp",EDGE,"E13.27.0"),sQuery(id+"F1.wireOp",EDGE,"E13.27.1"),sQuery(id+"F1.wireOp",EDGE,"E13.27.2"),sQuery(id+"F1.wireOp",EDGE,"E13.27.3"),sQuery(id+"F1.wireOp",EDGE,"E13.27.4"),sQuery(id+"F1.wireOp",EDGE,"E13.27.5"),sQuery(id+"F1.wireOp",EDGE,"E13.27.6"),sQuery(id+"F1.wireOp",EDGE,"E13.27.7"),sQuery(id+"F1.wireOp",EDGE,"E13.27.8"),sQuery(id+"F1.wireOp",EDGE,"E13.27.9"),sQuery(id+"F1.wireOp",EDGE,"E13.27.10"),sQuery(id+"F1.wireOp",EDGE,"E13.27.12"),sQuery(id+"F1.wireOp",EDGE,"E13.28.0"),sQuery(id+"F1.wireOp",EDGE,"E13.28.1"),sQuery(id+"F1.wireOp",EDGE,"E13.28.2"),sQuery(id+"F1.wireOp",EDGE,"E13.28.3"),sQuery(id+"F1.wireOp",EDGE,"E13.28.4"),sQuery(id+"F1.wireOp",EDGE,"E13.28.5"),sQuery(id+"F1.wireOp",EDGE,"E13.28.6"),sQuery(id+"F1.wireOp",EDGE,"E13.28.7"),sQuery(id+"F1.wireOp",EDGE,"E13.28.8"),sQuery(id+"F1.wireOp",EDGE,"E13.28.9"),sQuery(id+"F1.wireOp",EDGE,"E13.28.10"),sQuery(id+"F1.wireOp",EDGE,"E13.28.12"),sQuery(id+"F1.wireOp",EDGE,"E13.29.0"),sQuery(id+"F1.wireOp",EDGE,"E13.29.1"),sQuery(id+"F1.wireOp",EDGE,"E13.29.2"),sQuery(id+"F1.wireOp",EDGE,"E13.29.3"),sQuery(id+"F1.wireOp",EDGE,"E13.29.4"),sQuery(id+"F1.wireOp",EDGE,"E13.29.5"),sQuery(id+"F1.wireOp",EDGE,"E13.29.6"),sQuery(id+"F1.wireOp",EDGE,"E13.29.7"),sQuery(id+"F1.wireOp",EDGE,"E13.29.8"),sQuery(id+"F1.wireOp",EDGE,"E13.29.9"),sQuery(id+"F1.wireOp",EDGE,"E13.29.10"),sQuery(id+"F1.wireOp",EDGE,"E13.29.12"),sQuery(id+"F1.wireOp",EDGE,"E13.30.0"),sQuery(id+"F1.wireOp",EDGE,"E13.30.1"),sQuery(id+"F1.wireOp",EDGE,"E13.30.2"),sQuery(id+"F1.wireOp",EDGE,"E13.30.3"),sQuery(id+"F1.wireOp",EDGE,"E13.30.4"),sQuery(id+"F1.wireOp",EDGE,"E13.30.5"),sQuery(id+"F1.wireOp",EDGE,"E13.30.6"),sQuery(id+"F1.wireOp",EDGE,"E13.30.7"),sQuery(id+"F1.wireOp",EDGE,"E13.30.8"),sQuery(id+"F1.wireOp",EDGE,"E13.30.9"),sQuery(id+"F1.wireOp",EDGE,"E13.30.10"),sQuery(id+"F1.wireOp",EDGE,"E13.30.12"),sQuery(id+"F1.wireOp",EDGE,"E13.31.0"),sQuery(id+"F1.wireOp",EDGE,"E13.31.1"),sQuery(id+"F1.wireOp",EDGE,"E13.31.2"),sQuery(id+"F1.wireOp",EDGE,"E13.31.3"),sQuery(id+"F1.wireOp",EDGE,"E13.31.4"),sQuery(id+"F1.wireOp",EDGE,"E13.31.5"),sQuery(id+"F1.wireOp",EDGE,"E13.31.6"),sQuery(id+"F1.wireOp",EDGE,"E13.31.7"),sQuery(id+"F1.wireOp",EDGE,"E13.31.8"),sQuery(id+"F1.wireOp",EDGE,"E13.31.9"),sQuery(id+"F1.wireOp",EDGE,"E13.31.10"),sQuery(id+"F1.wireOp",EDGE,"E13.31.12"),sQuery(id+"F1.wireOp",EDGE,"E13.32.0"),sQuery(id+"F1.wireOp",EDGE,"E13.32.1"),sQuery(id+"F1.wireOp",EDGE,"E13.32.2"),sQuery(id+"F1.wireOp",EDGE,"E13.32.3"),sQuery(id+"F1.wireOp",EDGE,"E13.32.4"),sQuery(id+"F1.wireOp",EDGE,"E13.32.5"),sQuery(id+"F1.wireOp",EDGE,"E13.32.6"),sQuery(id+"F1.wireOp",EDGE,"E13.32.7"),sQuery(id+"F1.wireOp",EDGE,"E13.32.8"),sQuery(id+"F1.wireOp",EDGE,"E13.32.9"),sQuery(id+"F1.wireOp",EDGE,"E13.32.10"),sQuery(id+"F1.wireOp",EDGE,"E13.32.12"),sQuery(id+"F1.wireOp",EDGE,"E13.33.0"),sQuery(id+"F1.wireOp",EDGE,"E13.33.1"),sQuery(id+"F1.wireOp",EDGE,"E13.33.2"),sQuery(id+"F1.wireOp",EDGE,"E13.33.3"),sQuery(id+"F1.wireOp",EDGE,"E13.33.4"),sQuery(id+"F1.wireOp",EDGE,"E13.33.5"),sQuery(id+"F1.wireOp",EDGE,"E13.33.6"),sQuery(id+"F1.wireOp",EDGE,"E13.33.7"),sQuery(id+"F1.wireOp",EDGE,"E13.33.8"),sQuery(id+"F1.wireOp",EDGE,"E13.33.9"),sQuery(id+"F1.wireOp",EDGE,"E13.33.10"),sQuery(id+"F1.wireOp",EDGE,"E13.33.12"),sQuery(id+"F1.wireOp",EDGE,"E13.34.0"),sQuery(id+"F1.wireOp",EDGE,"E13.34.1"),sQuery(id+"F1.wireOp",EDGE,"E13.34.2"),sQuery(id+"F1.wireOp",EDGE,"E13.34.3"),sQuery(id+"F1.wireOp",EDGE,"E13.34.4"),sQuery(id+"F1.wireOp",EDGE,"E13.34.5"),sQuery(id+"F1.wireOp",EDGE,"E13.34.6"),sQuery(id+"F1.wireOp",EDGE,"E13.34.7"),sQuery(id+"F1.wireOp",EDGE,"E13.34.8"),sQuery(id+"F1.wireOp",EDGE,"E13.34.9"),sQuery(id+"F1.wireOp",EDGE,"E13.34.10"),sQuery(id+"F1.wireOp",EDGE,"E13.34.12"),sQuery(id+"F1.wireOp",EDGE,"E13.35.0"),sQuery(id+"F1.wireOp",EDGE,"E13.35.1"),sQuery(id+"F1.wireOp",EDGE,"E13.35.2"),sQuery(id+"F1.wireOp",EDGE,"E13.35.3"),sQuery(id+"F1.wireOp",EDGE,"E13.35.4"),sQuery(id+"F1.wireOp",EDGE,"E13.35.5"),sQuery(id+"F1.wireOp",EDGE,"E13.35.6"),sQuery(id+"F1.wireOp",EDGE,"E13.35.7"),sQuery(id+"F1.wireOp",EDGE,"E13.35.8"),sQuery(id+"F1.wireOp",EDGE,"E13.35.9"),sQuery(id+"F1.wireOp",EDGE,"E13.35.10"),sQuery(id+"F1.wireOp",EDGE,"E13.35.12"),sQuery(id+"F1.wireOp",EDGE,"E14.trimOffspring"),sQuery(id+"F1.wireOp",EDGE,"E15.trimOffspring"),sQuery(id+"F1.wireOp",EDGE,"E16.trimOffspring"),sQuery(id+"F1.wireOp",EDGE,"E17.trimOffspring"),sQuery(id+"F1.wireOp",EDGE,"E18.trimOffspring"),sQuery(id+"F1.wireOp",EDGE,"E19.trimOffspring"),sQuery(id+"F1.wireOp",EDGE,"E20.trimOffspring"),sQuery(id+"F1.wireOp",EDGE,"E21.trimOffspring"),sQuery(id+"F1.wireOp",EDGE,"E22.trimOffspring"),sQuery(id+"F1.wireOp",EDGE,"E23.trimOffspring"),sQuery(id+"F1.wireOp",EDGE,"E24.trimOffspring"),sQuery(id+"F1.wireOp",EDGE,"E25.trimOffspring"),sQuery(id+"F1.wireOp",EDGE,"E26.trimOffspring"),sQuery(id+"F1.wireOp",EDGE,"E27.trimOffspring"),sQuery(id+"F1.wireOp",EDGE,"E28.trimOffspring"),sQuery(id+"F1.wireOp",EDGE,"E29.trimOffspring"),sQuery(id+"F1.wireOp",EDGE,"E30.trimOffspring"),sQuery(id+"F1.wireOp",EDGE,"E31.trimOffspring"),sQuery(id+"F1.wireOp",EDGE,"E32.trimOffspring"),sQuery(id+"F1.wireOp",EDGE,"E33.trimOffspring"),sQuery(id+"F1.wireOp",EDGE,"E34.trimOffspring"),sQuery(id+"F1.wireOp",EDGE,"E35.trimOffspring"),sQuery(id+"F1.wireOp",EDGE,"E36.trimOffspring"),sQuery(id+"F1.wireOp",EDGE,"E37.trimOffspring"),sQuery(id+"F1.wireOp",EDGE,"E38.trimOffspring"),sQuery(id+"F1.wireOp",EDGE,"E39.trimOffspring"),sQuery(id+"F1.wireOp",EDGE,"E40.trimOffspring"),sQuery(id+"F1.wireOp",EDGE,"E41.trimOffspring"),sQuery(id+"F1.wireOp",EDGE,"E42.trimOffspring"),sQuery(id+"F1.wireOp",EDGE,"E43.trimOffspring"),sQuery(id+"F1.wireOp",EDGE,"E44.trimOffspring"),sQuery(id+"F1.wireOp",EDGE,"E45.trimOffspring"),sQuery(id+"F1.wireOp",EDGE,"E46.trimOffspring"),sQuery(id+"F1.wireOp",EDGE,"E47.trimOffspring"),sQuery(id+"F1.wireOp",EDGE,"E48.trimOffspring")])],"isStart":false});
            var sketch = newSketch(context, id + "F3", { "sketchPlane" : qUnion([Q0])});
            skCircle(sketch, "E49", {"center": v(0, 0) * mm, "radius": 3.18 * mm});
            skSolve(sketch);
        }
        {
            var Q0;
            Q0 = qSketchRegion(id + "F3", true);
            extrude(context, id + "F4", {"entities" : qUnion([Q0]), "operationType" : NewBodyOperationType.REMOVE, "endBound" : BoundingType.THROUGH_ALL, "oppositeDirection" : true, "depth" : 25.4 * mm});
        }
        {
            var Q0;
            Q0=makeQuery(id+"F2.opExtrude","CAP_FACE",FACE,{"disambiguationData":[OSD([sQuery(id+"F1.wireOp",EDGE,"E0"),sQuery(id+"F1.wireOp",EDGE,"E1.trimOffspring"),sQuery(id+"F1.wireOp",EDGE,"E2"),sQuery(id+"F1.wireOp",EDGE,"E3"),sQuery(id+"F1.wireOp",EDGE,"E4.MirrorCS"),sQuery(id+"F1.wireOp",EDGE,"E5.MirrorCS"),sQuery(id+"F1.wireOp",EDGE,"E6.MirrorCS"),sQuery(id+"F1.wireOp",EDGE,"E7.filletArc"),sQuery(id+"F1.wireOp",EDGE,"E8.filletArc"),sQuery(id+"F1.wireOp",EDGE,"E9.filletArc"),sQuery(id+"F1.wireOp",EDGE,"E10.filletArc"),sQuery(id+"F1.wireOp",EDGE,"E11.filletArc"),sQuery(id+"F1.wireOp",EDGE,"E12.filletArc"),sQuery(id+"F1.wireOp",EDGE,"E13.1.0"),sQuery(id+"F1.wireOp",EDGE,"E13.1.1"),sQuery(id+"F1.wireOp",EDGE,"E13.1.2"),sQuery(id+"F1.wireOp",EDGE,"E13.1.3"),sQuery(id+"F1.wireOp",EDGE,"E13.1.4"),sQuery(id+"F1.wireOp",EDGE,"E13.1.5"),sQuery(id+"F1.wireOp",EDGE,"E13.1.6"),sQuery(id+"F1.wireOp",EDGE,"E13.1.7"),sQuery(id+"F1.wireOp",EDGE,"E13.1.8"),sQuery(id+"F1.wireOp",EDGE,"E13.1.9"),sQuery(id+"F1.wireOp",EDGE,"E13.1.10"),sQuery(id+"F1.wireOp",EDGE,"E13.1.12"),sQuery(id+"F1.wireOp",EDGE,"E13.2.0"),sQuery(id+"F1.wireOp",EDGE,"E13.2.1"),sQuery(id+"F1.wireOp",EDGE,"E13.2.2"),sQuery(id+"F1.wireOp",EDGE,"E13.2.3"),sQuery(id+"F1.wireOp",EDGE,"E13.2.4"),sQuery(id+"F1.wireOp",EDGE,"E13.2.5"),sQuery(id+"F1.wireOp",EDGE,"E13.2.6"),sQuery(id+"F1.wireOp",EDGE,"E13.2.7"),sQuery(id+"F1.wireOp",EDGE,"E13.2.8"),sQuery(id+"F1.wireOp",EDGE,"E13.2.9"),sQuery(id+"F1.wireOp",EDGE,"E13.2.10"),sQuery(id+"F1.wireOp",EDGE,"E13.2.12"),sQuery(id+"F1.wireOp",EDGE,"E13.3.0"),sQuery(id+"F1.wireOp",EDGE,"E13.3.1"),sQuery(id+"F1.wireOp",EDGE,"E13.3.2"),sQuery(id+"F1.wireOp",EDGE,"E13.3.3"),sQuery(id+"F1.wireOp",EDGE,"E13.3.4"),sQuery(id+"F1.wireOp",EDGE,"E13.3.5"),sQuery(id+"F1.wireOp",EDGE,"E13.3.6"),sQuery(id+"F1.wireOp",EDGE,"E13.3.7"),sQuery(id+"F1.wireOp",EDGE,"E13.3.8"),sQuery(id+"F1.wireOp",EDGE,"E13.3.9"),sQuery(id+"F1.wireOp",EDGE,"E13.3.10"),sQuery(id+"F1.wireOp",EDGE,"E13.3.12"),sQuery(id+"F1.wireOp",EDGE,"E13.4.0"),sQuery(id+"F1.wireOp",EDGE,"E13.4.1"),sQuery(id+"F1.wireOp",EDGE,"E13.4.2"),sQuery(id+"F1.wireOp",EDGE,"E13.4.3"),sQuery(id+"F1.wireOp",EDGE,"E13.4.4"),sQuery(id+"F1.wireOp",EDGE,"E13.4.5"),sQuery(id+"F1.wireOp",EDGE,"E13.4.6"),sQuery(id+"F1.wireOp",EDGE,"E13.4.7"),sQuery(id+"F1.wireOp",EDGE,"E13.4.8"),sQuery(id+"F1.wireOp",EDGE,"E13.4.9"),sQuery(id+"F1.wireOp",EDGE,"E13.4.10"),sQuery(id+"F1.wireOp",EDGE,"E13.4.12"),sQuery(id+"F1.wireOp",EDGE,"E13.5.0"),sQuery(id+"F1.wireOp",EDGE,"E13.5.1"),sQuery(id+"F1.wireOp",EDGE,"E13.5.2"),sQuery(id+"F1.wireOp",EDGE,"E13.5.3"),sQuery(id+"F1.wireOp",EDGE,"E13.5.4"),sQuery(id+"F1.wireOp",EDGE,"E13.5.5"),sQuery(id+"F1.wireOp",EDGE,"E13.5.6"),sQuery(id+"F1.wireOp",EDGE,"E13.5.7"),sQuery(id+"F1.wireOp",EDGE,"E13.5.8"),sQuery(id+"F1.wireOp",EDGE,"E13.5.9"),sQuery(id+"F1.wireOp",EDGE,"E13.5.10"),sQuery(id+"F1.wireOp",EDGE,"E13.5.12"),sQuery(id+"F1.wireOp",EDGE,"E13.6.0"),sQuery(id+"F1.wireOp",EDGE,"E13.6.1"),sQuery(id+"F1.wireOp",EDGE,"E13.6.2"),sQuery(id+"F1.wireOp",EDGE,"E13.6.3"),sQuery(id+"F1.wireOp",EDGE,"E13.6.4"),sQuery(id+"F1.wireOp",EDGE,"E13.6.5"),sQuery(id+"F1.wireOp",EDGE,"E13.6.6"),sQuery(id+"F1.wireOp",EDGE,"E13.6.7"),sQuery(id+"F1.wireOp",EDGE,"E13.6.8"),sQuery(id+"F1.wireOp",EDGE,"E13.6.9"),sQuery(id+"F1.wireOp",EDGE,"E13.6.10"),sQuery(id+"F1.wireOp",EDGE,"E13.6.12"),sQuery(id+"F1.wireOp",EDGE,"E13.7.0"),sQuery(id+"F1.wireOp",EDGE,"E13.7.1"),sQuery(id+"F1.wireOp",EDGE,"E13.7.2"),sQuery(id+"F1.wireOp",EDGE,"E13.7.3"),sQuery(id+"F1.wireOp",EDGE,"E13.7.4"),sQuery(id+"F1.wireOp",EDGE,"E13.7.5"),sQuery(id+"F1.wireOp",EDGE,"E13.7.6"),sQuery(id+"F1.wireOp",EDGE,"E13.7.7"),sQuery(id+"F1.wireOp",EDGE,"E13.7.8"),sQuery(id+"F1.wireOp",EDGE,"E13.7.9"),sQuery(id+"F1.wireOp",EDGE,"E13.7.10"),sQuery(id+"F1.wireOp",EDGE,"E13.7.12"),sQuery(id+"F1.wireOp",EDGE,"E13.8.0"),sQuery(id+"F1.wireOp",EDGE,"E13.8.1"),sQuery(id+"F1.wireOp",EDGE,"E13.8.2"),sQuery(id+"F1.wireOp",EDGE,"E13.8.3"),sQuery(id+"F1.wireOp",EDGE,"E13.8.4"),sQuery(id+"F1.wireOp",EDGE,"E13.8.5"),sQuery(id+"F1.wireOp",EDGE,"E13.8.6"),sQuery(id+"F1.wireOp",EDGE,"E13.8.7"),sQuery(id+"F1.wireOp",EDGE,"E13.8.8"),sQuery(id+"F1.wireOp",EDGE,"E13.8.9"),sQuery(id+"F1.wireOp",EDGE,"E13.8.10"),sQuery(id+"F1.wireOp",EDGE,"E13.8.12"),sQuery(id+"F1.wireOp",EDGE,"E13.9.0"),sQuery(id+"F1.wireOp",EDGE,"E13.9.1"),sQuery(id+"F1.wireOp",EDGE,"E13.9.2"),sQuery(id+"F1.wireOp",EDGE,"E13.9.3"),sQuery(id+"F1.wireOp",EDGE,"E13.9.4"),sQuery(id+"F1.wireOp",EDGE,"E13.9.5"),sQuery(id+"F1.wireOp",EDGE,"E13.9.6"),sQuery(id+"F1.wireOp",EDGE,"E13.9.7"),sQuery(id+"F1.wireOp",EDGE,"E13.9.8"),sQuery(id+"F1.wireOp",EDGE,"E13.9.9"),sQuery(id+"F1.wireOp",EDGE,"E13.9.10"),sQuery(id+"F1.wireOp",EDGE,"E13.9.12"),sQuery(id+"F1.wireOp",EDGE,"E13.10.0"),sQuery(id+"F1.wireOp",EDGE,"E13.10.1"),sQuery(id+"F1.wireOp",EDGE,"E13.10.2"),sQuery(id+"F1.wireOp",EDGE,"E13.10.3"),sQuery(id+"F1.wireOp",EDGE,"E13.10.4"),sQuery(id+"F1.wireOp",EDGE,"E13.10.5"),sQuery(id+"F1.wireOp",EDGE,"E13.10.6"),sQuery(id+"F1.wireOp",EDGE,"E13.10.7"),sQuery(id+"F1.wireOp",EDGE,"E13.10.8"),sQuery(id+"F1.wireOp",EDGE,"E13.10.9"),sQuery(id+"F1.wireOp",EDGE,"E13.10.10"),sQuery(id+"F1.wireOp",EDGE,"E13.10.12"),sQuery(id+"F1.wireOp",EDGE,"E13.11.0"),sQuery(id+"F1.wireOp",EDGE,"E13.11.1"),sQuery(id+"F1.wireOp",EDGE,"E13.11.2"),sQuery(id+"F1.wireOp",EDGE,"E13.11.3"),sQuery(id+"F1.wireOp",EDGE,"E13.11.4"),sQuery(id+"F1.wireOp",EDGE,"E13.11.5"),sQuery(id+"F1.wireOp",EDGE,"E13.11.6"),sQuery(id+"F1.wireOp",EDGE,"E13.11.7"),sQuery(id+"F1.wireOp",EDGE,"E13.11.8"),sQuery(id+"F1.wireOp",EDGE,"E13.11.9"),sQuery(id+"F1.wireOp",EDGE,"E13.11.10"),sQuery(id+"F1.wireOp",EDGE,"E13.11.12"),sQuery(id+"F1.wireOp",EDGE,"E13.12.0"),sQuery(id+"F1.wireOp",EDGE,"E13.12.1"),sQuery(id+"F1.wireOp",EDGE,"E13.12.2"),sQuery(id+"F1.wireOp",EDGE,"E13.12.3"),sQuery(id+"F1.wireOp",EDGE,"E13.12.4"),sQuery(id+"F1.wireOp",EDGE,"E13.12.5"),sQuery(id+"F1.wireOp",EDGE,"E13.12.6"),sQuery(id+"F1.wireOp",EDGE,"E13.12.7"),sQuery(id+"F1.wireOp",EDGE,"E13.12.8"),sQuery(id+"F1.wireOp",EDGE,"E13.12.9"),sQuery(id+"F1.wireOp",EDGE,"E13.12.10"),sQuery(id+"F1.wireOp",EDGE,"E13.12.12"),sQuery(id+"F1.wireOp",EDGE,"E13.13.0"),sQuery(id+"F1.wireOp",EDGE,"E13.13.1"),sQuery(id+"F1.wireOp",EDGE,"E13.13.2"),sQuery(id+"F1.wireOp",EDGE,"E13.13.3"),sQuery(id+"F1.wireOp",EDGE,"E13.13.4"),sQuery(id+"F1.wireOp",EDGE,"E13.13.5"),sQuery(id+"F1.wireOp",EDGE,"E13.13.6"),sQuery(id+"F1.wireOp",EDGE,"E13.13.7"),sQuery(id+"F1.wireOp",EDGE,"E13.13.8"),sQuery(id+"F1.wireOp",EDGE,"E13.13.9"),sQuery(id+"F1.wireOp",EDGE,"E13.13.10"),sQuery(id+"F1.wireOp",EDGE,"E13.13.12"),sQuery(id+"F1.wireOp",EDGE,"E13.14.0"),sQuery(id+"F1.wireOp",EDGE,"E13.14.1"),sQuery(id+"F1.wireOp",EDGE,"E13.14.2"),sQuery(id+"F1.wireOp",EDGE,"E13.14.3"),sQuery(id+"F1.wireOp",EDGE,"E13.14.4"),sQuery(id+"F1.wireOp",EDGE,"E13.14.5"),sQuery(id+"F1.wireOp",EDGE,"E13.14.6"),sQuery(id+"F1.wireOp",EDGE,"E13.14.7"),sQuery(id+"F1.wireOp",EDGE,"E13.14.8"),sQuery(id+"F1.wireOp",EDGE,"E13.14.9"),sQuery(id+"F1.wireOp",EDGE,"E13.14.10"),sQuery(id+"F1.wireOp",EDGE,"E13.14.12"),sQuery(id+"F1.wireOp",EDGE,"E13.15.0"),sQuery(id+"F1.wireOp",EDGE,"E13.15.1"),sQuery(id+"F1.wireOp",EDGE,"E13.15.2"),sQuery(id+"F1.wireOp",EDGE,"E13.15.3"),sQuery(id+"F1.wireOp",EDGE,"E13.15.4"),sQuery(id+"F1.wireOp",EDGE,"E13.15.5"),sQuery(id+"F1.wireOp",EDGE,"E13.15.6"),sQuery(id+"F1.wireOp",EDGE,"E13.15.7"),sQuery(id+"F1.wireOp",EDGE,"E13.15.8"),sQuery(id+"F1.wireOp",EDGE,"E13.15.9"),sQuery(id+"F1.wireOp",EDGE,"E13.15.10"),sQuery(id+"F1.wireOp",EDGE,"E13.15.12"),sQuery(id+"F1.wireOp",EDGE,"E13.16.0"),sQuery(id+"F1.wireOp",EDGE,"E13.16.1"),sQuery(id+"F1.wireOp",EDGE,"E13.16.2"),sQuery(id+"F1.wireOp",EDGE,"E13.16.3"),sQuery(id+"F1.wireOp",EDGE,"E13.16.4"),sQuery(id+"F1.wireOp",EDGE,"E13.16.5"),sQuery(id+"F1.wireOp",EDGE,"E13.16.6"),sQuery(id+"F1.wireOp",EDGE,"E13.16.7"),sQuery(id+"F1.wireOp",EDGE,"E13.16.8"),sQuery(id+"F1.wireOp",EDGE,"E13.16.9"),sQuery(id+"F1.wireOp",EDGE,"E13.16.10"),sQuery(id+"F1.wireOp",EDGE,"E13.16.12"),sQuery(id+"F1.wireOp",EDGE,"E13.17.0"),sQuery(id+"F1.wireOp",EDGE,"E13.17.1"),sQuery(id+"F1.wireOp",EDGE,"E13.17.2"),sQuery(id+"F1.wireOp",EDGE,"E13.17.3"),sQuery(id+"F1.wireOp",EDGE,"E13.17.4"),sQuery(id+"F1.wireOp",EDGE,"E13.17.5"),sQuery(id+"F1.wireOp",EDGE,"E13.17.6"),sQuery(id+"F1.wireOp",EDGE,"E13.17.7"),sQuery(id+"F1.wireOp",EDGE,"E13.17.8"),sQuery(id+"F1.wireOp",EDGE,"E13.17.9"),sQuery(id+"F1.wireOp",EDGE,"E13.17.10"),sQuery(id+"F1.wireOp",EDGE,"E13.17.12"),sQuery(id+"F1.wireOp",EDGE,"E13.18.0"),sQuery(id+"F1.wireOp",EDGE,"E13.18.1"),sQuery(id+"F1.wireOp",EDGE,"E13.18.2"),sQuery(id+"F1.wireOp",EDGE,"E13.18.3"),sQuery(id+"F1.wireOp",EDGE,"E13.18.4"),sQuery(id+"F1.wireOp",EDGE,"E13.18.5"),sQuery(id+"F1.wireOp",EDGE,"E13.18.6"),sQuery(id+"F1.wireOp",EDGE,"E13.18.7"),sQuery(id+"F1.wireOp",EDGE,"E13.18.8"),sQuery(id+"F1.wireOp",EDGE,"E13.18.9"),sQuery(id+"F1.wireOp",EDGE,"E13.18.10"),sQuery(id+"F1.wireOp",EDGE,"E13.18.12"),sQuery(id+"F1.wireOp",EDGE,"E13.19.0"),sQuery(id+"F1.wireOp",EDGE,"E13.19.1"),sQuery(id+"F1.wireOp",EDGE,"E13.19.2"),sQuery(id+"F1.wireOp",EDGE,"E13.19.3"),sQuery(id+"F1.wireOp",EDGE,"E13.19.4"),sQuery(id+"F1.wireOp",EDGE,"E13.19.5"),sQuery(id+"F1.wireOp",EDGE,"E13.19.6"),sQuery(id+"F1.wireOp",EDGE,"E13.19.7"),sQuery(id+"F1.wireOp",EDGE,"E13.19.8"),sQuery(id+"F1.wireOp",EDGE,"E13.19.9"),sQuery(id+"F1.wireOp",EDGE,"E13.19.10"),sQuery(id+"F1.wireOp",EDGE,"E13.19.12"),sQuery(id+"F1.wireOp",EDGE,"E13.20.0"),sQuery(id+"F1.wireOp",EDGE,"E13.20.1"),sQuery(id+"F1.wireOp",EDGE,"E13.20.2"),sQuery(id+"F1.wireOp",EDGE,"E13.20.3"),sQuery(id+"F1.wireOp",EDGE,"E13.20.4"),sQuery(id+"F1.wireOp",EDGE,"E13.20.5"),sQuery(id+"F1.wireOp",EDGE,"E13.20.6"),sQuery(id+"F1.wireOp",EDGE,"E13.20.7"),sQuery(id+"F1.wireOp",EDGE,"E13.20.8"),sQuery(id+"F1.wireOp",EDGE,"E13.20.9"),sQuery(id+"F1.wireOp",EDGE,"E13.20.10"),sQuery(id+"F1.wireOp",EDGE,"E13.20.12"),sQuery(id+"F1.wireOp",EDGE,"E13.21.0"),sQuery(id+"F1.wireOp",EDGE,"E13.21.1"),sQuery(id+"F1.wireOp",EDGE,"E13.21.2"),sQuery(id+"F1.wireOp",EDGE,"E13.21.3"),sQuery(id+"F1.wireOp",EDGE,"E13.21.4"),sQuery(id+"F1.wireOp",EDGE,"E13.21.5"),sQuery(id+"F1.wireOp",EDGE,"E13.21.6"),sQuery(id+"F1.wireOp",EDGE,"E13.21.7"),sQuery(id+"F1.wireOp",EDGE,"E13.21.8"),sQuery(id+"F1.wireOp",EDGE,"E13.21.9"),sQuery(id+"F1.wireOp",EDGE,"E13.21.10"),sQuery(id+"F1.wireOp",EDGE,"E13.21.12"),sQuery(id+"F1.wireOp",EDGE,"E13.22.0"),sQuery(id+"F1.wireOp",EDGE,"E13.22.1"),sQuery(id+"F1.wireOp",EDGE,"E13.22.2"),sQuery(id+"F1.wireOp",EDGE,"E13.22.3"),sQuery(id+"F1.wireOp",EDGE,"E13.22.4"),sQuery(id+"F1.wireOp",EDGE,"E13.22.5"),sQuery(id+"F1.wireOp",EDGE,"E13.22.6"),sQuery(id+"F1.wireOp",EDGE,"E13.22.7"),sQuery(id+"F1.wireOp",EDGE,"E13.22.8"),sQuery(id+"F1.wireOp",EDGE,"E13.22.9"),sQuery(id+"F1.wireOp",EDGE,"E13.22.10"),sQuery(id+"F1.wireOp",EDGE,"E13.22.12"),sQuery(id+"F1.wireOp",EDGE,"E13.23.0"),sQuery(id+"F1.wireOp",EDGE,"E13.23.1"),sQuery(id+"F1.wireOp",EDGE,"E13.23.2"),sQuery(id+"F1.wireOp",EDGE,"E13.23.3"),sQuery(id+"F1.wireOp",EDGE,"E13.23.4"),sQuery(id+"F1.wireOp",EDGE,"E13.23.5"),sQuery(id+"F1.wireOp",EDGE,"E13.23.6"),sQuery(id+"F1.wireOp",EDGE,"E13.23.7"),sQuery(id+"F1.wireOp",EDGE,"E13.23.8"),sQuery(id+"F1.wireOp",EDGE,"E13.23.9"),sQuery(id+"F1.wireOp",EDGE,"E13.23.10"),sQuery(id+"F1.wireOp",EDGE,"E13.23.12"),sQuery(id+"F1.wireOp",EDGE,"E13.24.0"),sQuery(id+"F1.wireOp",EDGE,"E13.24.1"),sQuery(id+"F1.wireOp",EDGE,"E13.24.2"),sQuery(id+"F1.wireOp",EDGE,"E13.24.3"),sQuery(id+"F1.wireOp",EDGE,"E13.24.4"),sQuery(id+"F1.wireOp",EDGE,"E13.24.5"),sQuery(id+"F1.wireOp",EDGE,"E13.24.6"),sQuery(id+"F1.wireOp",EDGE,"E13.24.7"),sQuery(id+"F1.wireOp",EDGE,"E13.24.8"),sQuery(id+"F1.wireOp",EDGE,"E13.24.9"),sQuery(id+"F1.wireOp",EDGE,"E13.24.10"),sQuery(id+"F1.wireOp",EDGE,"E13.24.12"),sQuery(id+"F1.wireOp",EDGE,"E13.25.0"),sQuery(id+"F1.wireOp",EDGE,"E13.25.1"),sQuery(id+"F1.wireOp",EDGE,"E13.25.2"),sQuery(id+"F1.wireOp",EDGE,"E13.25.3"),sQuery(id+"F1.wireOp",EDGE,"E13.25.4"),sQuery(id+"F1.wireOp",EDGE,"E13.25.5"),sQuery(id+"F1.wireOp",EDGE,"E13.25.6"),sQuery(id+"F1.wireOp",EDGE,"E13.25.7"),sQuery(id+"F1.wireOp",EDGE,"E13.25.8"),sQuery(id+"F1.wireOp",EDGE,"E13.25.9"),sQuery(id+"F1.wireOp",EDGE,"E13.25.10"),sQuery(id+"F1.wireOp",EDGE,"E13.25.12"),sQuery(id+"F1.wireOp",EDGE,"E13.26.0"),sQuery(id+"F1.wireOp",EDGE,"E13.26.1"),sQuery(id+"F1.wireOp",EDGE,"E13.26.2"),sQuery(id+"F1.wireOp",EDGE,"E13.26.3"),sQuery(id+"F1.wireOp",EDGE,"E13.26.4"),sQuery(id+"F1.wireOp",EDGE,"E13.26.5"),sQuery(id+"F1.wireOp",EDGE,"E13.26.6"),sQuery(id+"F1.wireOp",EDGE,"E13.26.7"),sQuery(id+"F1.wireOp",EDGE,"E13.26.8"),sQuery(id+"F1.wireOp",EDGE,"E13.26.9"),sQuery(id+"F1.wireOp",EDGE,"E13.26.10"),sQuery(id+"F1.wireOp",EDGE,"E13.26.12"),sQuery(id+"F1.wireOp",EDGE,"E13.27.0"),sQuery(id+"F1.wireOp",EDGE,"E13.27.1"),sQuery(id+"F1.wireOp",EDGE,"E13.27.2"),sQuery(id+"F1.wireOp",EDGE,"E13.27.3"),sQuery(id+"F1.wireOp",EDGE,"E13.27.4"),sQuery(id+"F1.wireOp",EDGE,"E13.27.5"),sQuery(id+"F1.wireOp",EDGE,"E13.27.6"),sQuery(id+"F1.wireOp",EDGE,"E13.27.7"),sQuery(id+"F1.wireOp",EDGE,"E13.27.8"),sQuery(id+"F1.wireOp",EDGE,"E13.27.9"),sQuery(id+"F1.wireOp",EDGE,"E13.27.10"),sQuery(id+"F1.wireOp",EDGE,"E13.27.12"),sQuery(id+"F1.wireOp",EDGE,"E13.28.0"),sQuery(id+"F1.wireOp",EDGE,"E13.28.1"),sQuery(id+"F1.wireOp",EDGE,"E13.28.2"),sQuery(id+"F1.wireOp",EDGE,"E13.28.3"),sQuery(id+"F1.wireOp",EDGE,"E13.28.4"),sQuery(id+"F1.wireOp",EDGE,"E13.28.5"),sQuery(id+"F1.wireOp",EDGE,"E13.28.6"),sQuery(id+"F1.wireOp",EDGE,"E13.28.7"),sQuery(id+"F1.wireOp",EDGE,"E13.28.8"),sQuery(id+"F1.wireOp",EDGE,"E13.28.9"),sQuery(id+"F1.wireOp",EDGE,"E13.28.10"),sQuery(id+"F1.wireOp",EDGE,"E13.28.12"),sQuery(id+"F1.wireOp",EDGE,"E13.29.0"),sQuery(id+"F1.wireOp",EDGE,"E13.29.1"),sQuery(id+"F1.wireOp",EDGE,"E13.29.2"),sQuery(id+"F1.wireOp",EDGE,"E13.29.3"),sQuery(id+"F1.wireOp",EDGE,"E13.29.4"),sQuery(id+"F1.wireOp",EDGE,"E13.29.5"),sQuery(id+"F1.wireOp",EDGE,"E13.29.6"),sQuery(id+"F1.wireOp",EDGE,"E13.29.7"),sQuery(id+"F1.wireOp",EDGE,"E13.29.8"),sQuery(id+"F1.wireOp",EDGE,"E13.29.9"),sQuery(id+"F1.wireOp",EDGE,"E13.29.10"),sQuery(id+"F1.wireOp",EDGE,"E13.29.12"),sQuery(id+"F1.wireOp",EDGE,"E13.30.0"),sQuery(id+"F1.wireOp",EDGE,"E13.30.1"),sQuery(id+"F1.wireOp",EDGE,"E13.30.2"),sQuery(id+"F1.wireOp",EDGE,"E13.30.3"),sQuery(id+"F1.wireOp",EDGE,"E13.30.4"),sQuery(id+"F1.wireOp",EDGE,"E13.30.5"),sQuery(id+"F1.wireOp",EDGE,"E13.30.6"),sQuery(id+"F1.wireOp",EDGE,"E13.30.7"),sQuery(id+"F1.wireOp",EDGE,"E13.30.8"),sQuery(id+"F1.wireOp",EDGE,"E13.30.9"),sQuery(id+"F1.wireOp",EDGE,"E13.30.10"),sQuery(id+"F1.wireOp",EDGE,"E13.30.12"),sQuery(id+"F1.wireOp",EDGE,"E13.31.0"),sQuery(id+"F1.wireOp",EDGE,"E13.31.1"),sQuery(id+"F1.wireOp",EDGE,"E13.31.2"),sQuery(id+"F1.wireOp",EDGE,"E13.31.3"),sQuery(id+"F1.wireOp",EDGE,"E13.31.4"),sQuery(id+"F1.wireOp",EDGE,"E13.31.5"),sQuery(id+"F1.wireOp",EDGE,"E13.31.6"),sQuery(id+"F1.wireOp",EDGE,"E13.31.7"),sQuery(id+"F1.wireOp",EDGE,"E13.31.8"),sQuery(id+"F1.wireOp",EDGE,"E13.31.9"),sQuery(id+"F1.wireOp",EDGE,"E13.31.10"),sQuery(id+"F1.wireOp",EDGE,"E13.31.12"),sQuery(id+"F1.wireOp",EDGE,"E13.32.0"),sQuery(id+"F1.wireOp",EDGE,"E13.32.1"),sQuery(id+"F1.wireOp",EDGE,"E13.32.2"),sQuery(id+"F1.wireOp",EDGE,"E13.32.3"),sQuery(id+"F1.wireOp",EDGE,"E13.32.4"),sQuery(id+"F1.wireOp",EDGE,"E13.32.5"),sQuery(id+"F1.wireOp",EDGE,"E13.32.6"),sQuery(id+"F1.wireOp",EDGE,"E13.32.7"),sQuery(id+"F1.wireOp",EDGE,"E13.32.8"),sQuery(id+"F1.wireOp",EDGE,"E13.32.9"),sQuery(id+"F1.wireOp",EDGE,"E13.32.10"),sQuery(id+"F1.wireOp",EDGE,"E13.32.12"),sQuery(id+"F1.wireOp",EDGE,"E13.33.0"),sQuery(id+"F1.wireOp",EDGE,"E13.33.1"),sQuery(id+"F1.wireOp",EDGE,"E13.33.2"),sQuery(id+"F1.wireOp",EDGE,"E13.33.3"),sQuery(id+"F1.wireOp",EDGE,"E13.33.4"),sQuery(id+"F1.wireOp",EDGE,"E13.33.5"),sQuery(id+"F1.wireOp",EDGE,"E13.33.6"),sQuery(id+"F1.wireOp",EDGE,"E13.33.7"),sQuery(id+"F1.wireOp",EDGE,"E13.33.8"),sQuery(id+"F1.wireOp",EDGE,"E13.33.9"),sQuery(id+"F1.wireOp",EDGE,"E13.33.10"),sQuery(id+"F1.wireOp",EDGE,"E13.33.12"),sQuery(id+"F1.wireOp",EDGE,"E13.34.0"),sQuery(id+"F1.wireOp",EDGE,"E13.34.1"),sQuery(id+"F1.wireOp",EDGE,"E13.34.2"),sQuery(id+"F1.wireOp",EDGE,"E13.34.3"),sQuery(id+"F1.wireOp",EDGE,"E13.34.4"),sQuery(id+"F1.wireOp",EDGE,"E13.34.5"),sQuery(id+"F1.wireOp",EDGE,"E13.34.6"),sQuery(id+"F1.wireOp",EDGE,"E13.34.7"),sQuery(id+"F1.wireOp",EDGE,"E13.34.8"),sQuery(id+"F1.wireOp",EDGE,"E13.34.9"),sQuery(id+"F1.wireOp",EDGE,"E13.34.10"),sQuery(id+"F1.wireOp",EDGE,"E13.34.12"),sQuery(id+"F1.wireOp",EDGE,"E13.35.0"),sQuery(id+"F1.wireOp",EDGE,"E13.35.1"),sQuery(id+"F1.wireOp",EDGE,"E13.35.2"),sQuery(id+"F1.wireOp",EDGE,"E13.35.3"),sQuery(id+"F1.wireOp",EDGE,"E13.35.4"),sQuery(id+"F1.wireOp",EDGE,"E13.35.5"),sQuery(id+"F1.wireOp",EDGE,"E13.35.6"),sQuery(id+"F1.wireOp",EDGE,"E13.35.7"),sQuery(id+"F1.wireOp",EDGE,"E13.35.8"),sQuery(id+"F1.wireOp",EDGE,"E13.35.9"),sQuery(id+"F1.wireOp",EDGE,"E13.35.10"),sQuery(id+"F1.wireOp",EDGE,"E13.35.12"),sQuery(id+"F1.wireOp",EDGE,"E14.trimOffspring"),sQuery(id+"F1.wireOp",EDGE,"E15.trimOffspring"),sQuery(id+"F1.wireOp",EDGE,"E16.trimOffspring"),sQuery(id+"F1.wireOp",EDGE,"E17.trimOffspring"),sQuery(id+"F1.wireOp",EDGE,"E18.trimOffspring"),sQuery(id+"F1.wireOp",EDGE,"E19.trimOffspring"),sQuery(id+"F1.wireOp",EDGE,"E20.trimOffspring"),sQuery(id+"F1.wireOp",EDGE,"E21.trimOffspring"),sQuery(id+"F1.wireOp",EDGE,"E22.trimOffspring"),sQuery(id+"F1.wireOp",EDGE,"E23.trimOffspring"),sQuery(id+"F1.wireOp",EDGE,"E24.trimOffspring"),sQuery(id+"F1.wireOp",EDGE,"E25.trimOffspring"),sQuery(id+"F1.wireOp",EDGE,"E26.trimOffspring"),sQuery(id+"F1.wireOp",EDGE,"E27.trimOffspring"),sQuery(id+"F1.wireOp",EDGE,"E28.trimOffspring"),sQuery(id+"F1.wireOp",EDGE,"E29.trimOffspring"),sQuery(id+"F1.wireOp",EDGE,"E30.trimOffspring"),sQuery(id+"F1.wireOp",EDGE,"E31.trimOffspring"),sQuery(id+"F1.wireOp",EDGE,"E32.trimOffspring"),sQuery(id+"F1.wireOp",EDGE,"E33.trimOffspring"),sQuery(id+"F1.wireOp",EDGE,"E34.trimOffspring"),sQuery(id+"F1.wireOp",EDGE,"E35.trimOffspring"),sQuery(id+"F1.wireOp",EDGE,"E36.trimOffspring"),sQuery(id+"F1.wireOp",EDGE,"E37.trimOffspring"),sQuery(id+"F1.wireOp",EDGE,"E38.trimOffspring"),sQuery(id+"F1.wireOp",EDGE,"E39.trimOffspring"),sQuery(id+"F1.wireOp",EDGE,"E40.trimOffspring"),sQuery(id+"F1.wireOp",EDGE,"E41.trimOffspring"),sQuery(id+"F1.wireOp",EDGE,"E42.trimOffspring"),sQuery(id+"F1.wireOp",EDGE,"E43.trimOffspring"),sQuery(id+"F1.wireOp",EDGE,"E44.trimOffspring"),sQuery(id+"F1.wireOp",EDGE,"E45.trimOffspring"),sQuery(id+"F1.wireOp",EDGE,"E46.trimOffspring"),sQuery(id+"F1.wireOp",EDGE,"E47.trimOffspring"),sQuery(id+"F1.wireOp",EDGE,"E48.trimOffspring")])],"isStart":false});
            shell(context, id + "F5", {"entities" : qUnion([Q0]), "thickness" : 6.35 * mm});
        }
    });
